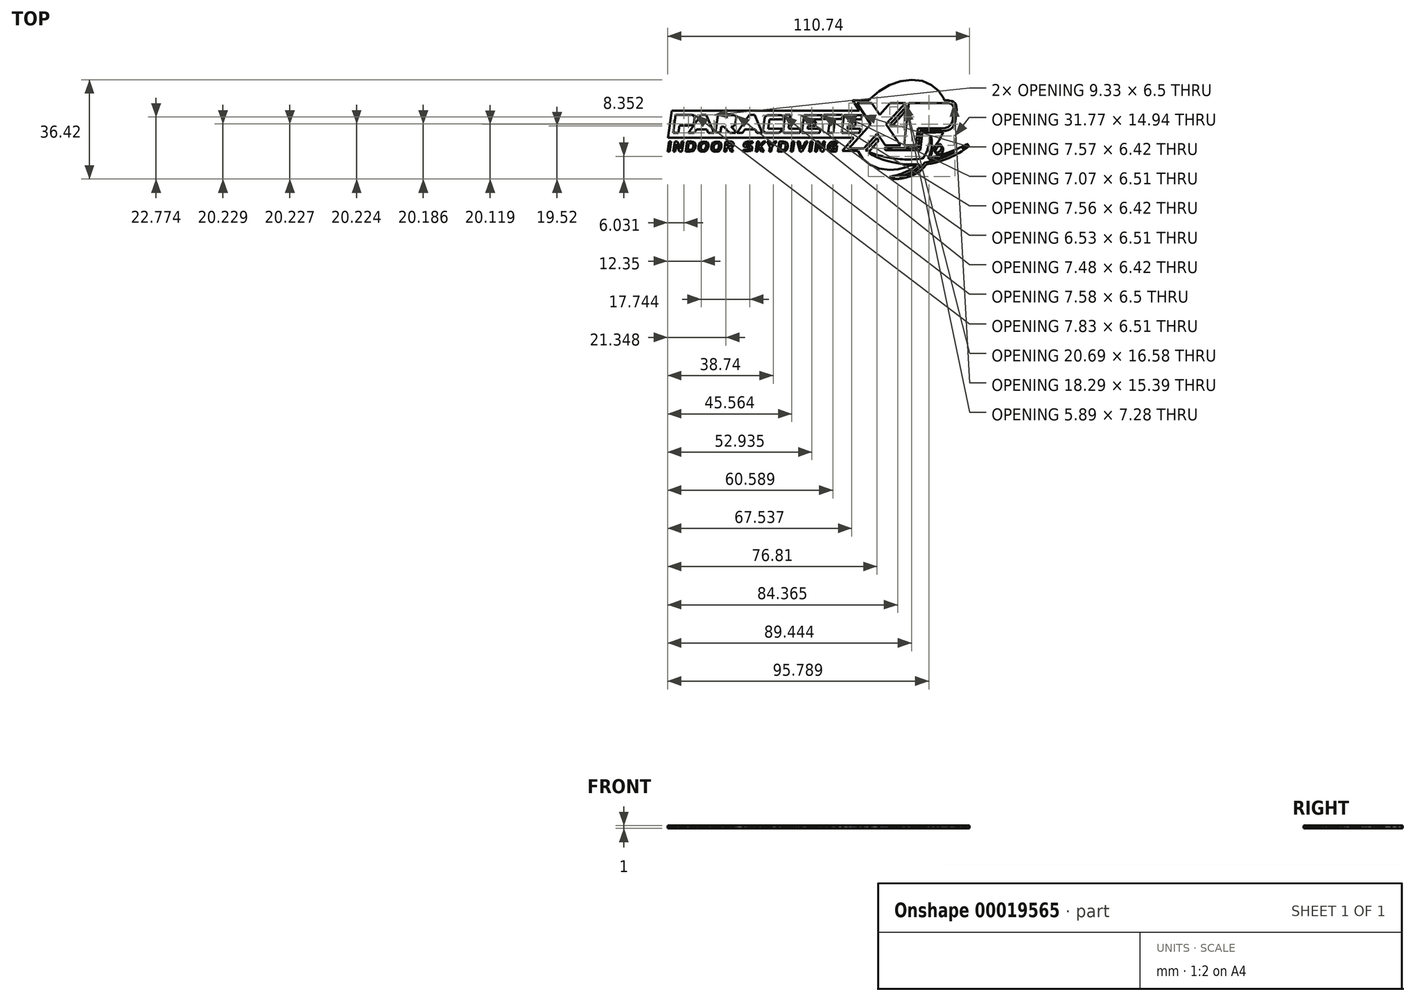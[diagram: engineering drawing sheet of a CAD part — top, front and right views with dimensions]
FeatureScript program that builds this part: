
annotation { "Feature Type Name" : "Feature", "Feature Type Description" : "" }
export const myFeature = defineFeature(function(context is Context, id is Id, definition is map)
    precondition{}
    {
        {
            var Q0;
            Q0=qCreatedBy(makeId("Top.planeOp"),FACE);
            var sketch = newSketch(context, id + "F0", { "sketchPlane" : qUnion([Q0])});
            skLineSegment(sketch, "E0", {"start": v(44.07, 4.06) * mm, "end": v(37.84, 4.06) * mm});
            skLineSegment(sketch, "E1", {"start": v(37.84, 4.06) * mm, "end": v(37.92, 4.76) * mm});
            skLineSegment(sketch, "E2", {"start": v(37.92, 4.76) * mm, "end": v(44.15, 4.76) * mm});
            skLineSegment(sketch, "E3", {"start": v(44.15, 4.76) * mm, "end": v(44.07, 4.06) * mm});
            skLineSegment(sketch, "E4", {"start": v(31.73, 6.48) * mm, "end": v(26.66, 0.92) * mm});
            skLineSegment(sketch, "E5", {"start": v(26.66, 0.92) * mm, "end": v(26.05, 1.81) * mm});
            skLineSegment(sketch, "E6", {"start": v(26.05, 1.81) * mm, "end": v(31.43, 7.64) * mm});
            skLineSegment(sketch, "E7", {"start": v(31.43, 7.64) * mm, "end": v(31.94, 8.2) * mm});
            skLineSegment(sketch, "E8", {"start": v(31.94, 8.2) * mm, "end": v(31.73, 6.48) * mm});
            skLineSegment(sketch, "E9", {"start": v(18.73, -7.82) * mm, "end": v(17.16, -7.8) * mm});
            skLineSegment(sketch, "E10", {"start": v(17.16, -7.8) * mm, "end": v(21.42, -3.2) * mm});
            skLineSegment(sketch, "E11", {"start": v(21.42, -3.2) * mm, "end": v(21.98, -4.02) * mm});
            skLineSegment(sketch, "E12", {"start": v(21.98, -4.02) * mm, "end": v(18.73, -7.82) * mm});
            skLineSegment(sketch, "E13", {"start": v(50.18, 9.35) * mm, "end": v(49.97, 9.6) * mm});
            skLineSegment(sketch, "E14", {"start": v(49.97, 9.6) * mm, "end": v(49.52, 9.98) * mm});
            skLineSegment(sketch, "E15", {"start": v(49.52, 9.98) * mm, "end": v(48.81, 10.37) * mm});
            skLineSegment(sketch, "E16", {"start": v(48.81, 10.37) * mm, "end": v(47.85, 10.6) * mm});
            skLineSegment(sketch, "E17", {"start": v(47.85, 10.6) * mm, "end": v(47.79, 10.6) * mm});
            skLineSegment(sketch, "E18", {"start": v(47.79, 10.6) * mm, "end": v(47.5, 10.6) * mm});
            skLineSegment(sketch, "E19", {"start": v(47.5, 10.6) * mm, "end": v(46.1, 10.64) * mm});
            skLineSegment(sketch, "E20", {"start": v(46.1, 10.64) * mm, "end": v(45.86, 11.32) * mm});
            skLineSegment(sketch, "E21", {"start": v(45.86, 11.32) * mm, "end": v(43.99, 14.14) * mm});
            skLineSegment(sketch, "E22", {"start": v(43.99, 14.14) * mm, "end": v(41.35, 16.31) * mm});
            skLineSegment(sketch, "E23", {"start": v(41.35, 16.31) * mm, "end": v(38.05, 17.72) * mm});
            skLineSegment(sketch, "E24", {"start": v(38.05, 17.72) * mm, "end": v(34.16, 18.21) * mm});
            skLineSegment(sketch, "E25", {"start": v(34.16, 18.21) * mm, "end": v(29.98, 17.7) * mm});
            skLineSegment(sketch, "E26", {"start": v(29.98, 17.7) * mm, "end": v(25.94, 16.25) * mm});
            skLineSegment(sketch, "E27", {"start": v(25.94, 16.25) * mm, "end": v(22.2, 14) * mm});
            skLineSegment(sketch, "E28", {"start": v(22.2, 14) * mm, "end": v(18.9, 11.11) * mm});
            skLineSegment(sketch, "E29", {"start": v(18.9, 11.11) * mm, "end": v(18.9, 11.11) * mm});
            skLineSegment(sketch, "E30", {"start": v(18.9, 11.11) * mm, "end": v(18.6, 10.65) * mm});
            skLineSegment(sketch, "E31", {"start": v(18.6, 10.65) * mm, "end": v(12.46, 10.63) * mm});
            skLineSegment(sketch, "E32", {"start": v(12.46, 10.63) * mm, "end": v(14.94, 6.88) * mm});
            skLineSegment(sketch, "E33", {"start": v(14.94, 6.88) * mm, "end": v(-53.8, 6.88) * mm});
            skLineSegment(sketch, "E34", {"start": v(-53.8, 6.88) * mm, "end": v(-55.18, -3) * mm});
            skLineSegment(sketch, "E35", {"start": v(-55.18, -3) * mm, "end": v(12.92, -3) * mm});
            skLineSegment(sketch, "E36", {"start": v(12.92, -3) * mm, "end": v(8.72, -7.94) * mm});
            skLineSegment(sketch, "E37", {"start": v(8.72, -7.94) * mm, "end": v(14.43, -7.94) * mm});
            skLineSegment(sketch, "E38", {"start": v(14.43, -7.94) * mm, "end": v(16.25, -10.8) * mm});
            skLineSegment(sketch, "E39", {"start": v(16.25, -10.8) * mm, "end": v(18.84, -12.99) * mm});
            skLineSegment(sketch, "E40", {"start": v(18.84, -12.99) * mm, "end": v(22.15, -14.38) * mm});
            skLineSegment(sketch, "E41", {"start": v(22.15, -14.38) * mm, "end": v(26.1, -14.87) * mm});
            skLineSegment(sketch, "E42", {"start": v(26.1, -14.87) * mm, "end": v(29.14, -14.6) * mm});
            skLineSegment(sketch, "E43", {"start": v(29.14, -14.6) * mm, "end": v(32.13, -13.8) * mm});
            skLineSegment(sketch, "E44", {"start": v(32.13, -13.8) * mm, "end": v(35.01, -12.55) * mm});
            skLineSegment(sketch, "E45", {"start": v(35.01, -12.55) * mm, "end": v(37.72, -10.88) * mm});
            skLineSegment(sketch, "E46", {"start": v(37.72, -10.88) * mm, "end": v(40.2, -8.85) * mm});
            skLineSegment(sketch, "E47", {"start": v(40.2, -8.85) * mm, "end": v(42.4, -6.5) * mm});
            skLineSegment(sketch, "E48", {"start": v(42.4, -6.5) * mm, "end": v(44.24, -3.9) * mm});
            skLineSegment(sketch, "E49", {"start": v(44.24, -3.9) * mm, "end": v(45.67, -1.08) * mm});
            skLineSegment(sketch, "E50", {"start": v(45.67, -1.08) * mm, "end": v(42.9, -1.08) * mm});
            skLineSegment(sketch, "E51", {"start": v(42.9, -1.08) * mm, "end": v(38, -1.1) * mm});
            skLineSegment(sketch, "E52", {"start": v(38, -1.1) * mm, "end": v(37.24, -7.58) * mm});
            skLineSegment(sketch, "E53", {"start": v(37.24, -7.58) * mm, "end": v(24.6, -7.58) * mm});
            skLineSegment(sketch, "E54", {"start": v(24.6, -7.58) * mm, "end": v(24.04, -6.88) * mm});
            skLineSegment(sketch, "E55", {"start": v(24.04, -6.88) * mm, "end": v(36.5, -6.88) * mm});
            skLineSegment(sketch, "E56", {"start": v(36.5, -6.88) * mm, "end": v(37.17, -0.53) * mm});
            skLineSegment(sketch, "E57", {"start": v(37.17, -0.53) * mm, "end": v(46.28, -0.53) * mm});
            skLineSegment(sketch, "E58", {"start": v(46.28, -0.53) * mm, "end": v(46.39, -0.53) * mm});
            skLineSegment(sketch, "E59", {"start": v(46.39, -0.53) * mm, "end": v(46.67, -0.51) * mm});
            skLineSegment(sketch, "E60", {"start": v(46.67, -0.51) * mm, "end": v(47.1, -0.44) * mm});
            skLineSegment(sketch, "E61", {"start": v(47.1, -0.44) * mm, "end": v(47.61, -0.28) * mm});
            skLineSegment(sketch, "E62", {"start": v(47.61, -0.28) * mm, "end": v(48.18, 0) * mm});
            skLineSegment(sketch, "E63", {"start": v(48.18, 0) * mm, "end": v(48.76, 0.43) * mm});
            skLineSegment(sketch, "E64", {"start": v(48.76, 0.43) * mm, "end": v(49.3, 1.05) * mm});
            skLineSegment(sketch, "E65", {"start": v(49.3, 1.05) * mm, "end": v(49.78, 1.89) * mm});
            skLineSegment(sketch, "E66", {"start": v(49.78, 1.89) * mm, "end": v(49.85, 2.07) * mm});
            skLineSegment(sketch, "E67", {"start": v(49.85, 2.07) * mm, "end": v(49.92, 2.23) * mm});
            skLineSegment(sketch, "E68", {"start": v(49.92, 2.23) * mm, "end": v(49.91, 2.22) * mm});
            skLineSegment(sketch, "E69", {"start": v(49.91, 2.22) * mm, "end": v(50.05, 2.78) * mm});
            skLineSegment(sketch, "E70", {"start": v(50.05, 2.78) * mm, "end": v(50.57, 7.29) * mm});
            skLineSegment(sketch, "E71", {"start": v(50.57, 7.29) * mm, "end": v(50.54, 8.36) * mm});
            skLineSegment(sketch, "E72", {"start": v(50.54, 8.36) * mm, "end": v(50.18, 9.35) * mm});
            skLineSegment(sketch, "E73", {"start": v(22.13, -1.6) * mm, "end": v(24.62, -5.2) * mm});
            skLineSegment(sketch, "E74", {"start": v(24.62, -5.2) * mm, "end": v(24.85, -5.3) * mm});
            skLineSegment(sketch, "E75", {"start": v(24.85, -5.3) * mm, "end": v(25.32, -5.3) * mm});
            skLineSegment(sketch, "E76", {"start": v(25.32, -5.3) * mm, "end": v(25, -4.84) * mm});
            skLineSegment(sketch, "E77", {"start": v(25, -4.84) * mm, "end": v(24.98, -4.84) * mm});
            skLineSegment(sketch, "E78", {"start": v(24.98, -4.84) * mm, "end": v(22.48, -1.22) * mm});
            skLineSegment(sketch, "E79", {"start": v(22.48, -1.22) * mm, "end": v(22.13, -1.6) * mm});
            skLineSegment(sketch, "E80", {"start": v(19.54, 8.64) * mm, "end": v(19.3, 9) * mm});
            skLineSegment(sketch, "E81", {"start": v(19.3, 9) * mm, "end": v(19.08, 9.12) * mm});
            skLineSegment(sketch, "E82", {"start": v(19.08, 9.12) * mm, "end": v(15.47, 9.12) * mm});
            skLineSegment(sketch, "E83", {"start": v(15.47, 9.12) * mm, "end": v(15.19, 8.96) * mm});
            skLineSegment(sketch, "E84", {"start": v(15.19, 8.96) * mm, "end": v(15.19, 8.64) * mm});
            skLineSegment(sketch, "E85", {"start": v(15.19, 8.64) * mm, "end": v(16.41, 6.85) * mm});
            skLineSegment(sketch, "E86", {"start": v(16.41, 6.85) * mm, "end": v(17.03, 6.85) * mm});
            skLineSegment(sketch, "E87", {"start": v(17.03, 6.85) * mm, "end": v(15.8, 8.64) * mm});
            skLineSegment(sketch, "E88", {"start": v(15.8, 8.64) * mm, "end": v(19.54, 8.64) * mm});
            skLineSegment(sketch, "E89", {"start": v(30.36, 8.64) * mm, "end": v(30.43, 8.96) * mm});
            skLineSegment(sketch, "E90", {"start": v(30.43, 8.96) * mm, "end": v(30.19, 9.12) * mm});
            skLineSegment(sketch, "E91", {"start": v(30.19, 9.12) * mm, "end": v(26.6, 9.12) * mm});
            skLineSegment(sketch, "E92", {"start": v(26.6, 9.12) * mm, "end": v(26.34, 9) * mm});
            skLineSegment(sketch, "E93", {"start": v(26.34, 9) * mm, "end": v(14.22, -4.18) * mm});
            skLineSegment(sketch, "E94", {"start": v(14.22, -4.18) * mm, "end": v(14.19, -4.45) * mm});
            skLineSegment(sketch, "E95", {"start": v(14.19, -4.45) * mm, "end": v(14.2, -4.48) * mm});
            skLineSegment(sketch, "E96", {"start": v(14.2, -4.48) * mm, "end": v(14.37, -4.56) * mm});
            skLineSegment(sketch, "E97", {"start": v(14.37, -4.56) * mm, "end": v(14.55, -4.48) * mm});
            skLineSegment(sketch, "E98", {"start": v(14.55, -4.48) * mm, "end": v(26.61, 8.64) * mm});
            skLineSegment(sketch, "E99", {"start": v(26.61, 8.64) * mm, "end": v(30.36, 8.64) * mm});
            skLineSegment(sketch, "E100", {"start": v(12.17, -5.78) * mm, "end": v(19.17, 1.9) * mm});
            skLineSegment(sketch, "E101", {"start": v(19.17, 1.9) * mm, "end": v(14.04, 9.6) * mm});
            skLineSegment(sketch, "E102", {"start": v(14.04, 9.6) * mm, "end": v(19.5, 9.6) * mm});
            skLineSegment(sketch, "E103", {"start": v(19.5, 9.6) * mm, "end": v(22.39, 5.38) * mm});
            skLineSegment(sketch, "E104", {"start": v(22.39, 5.38) * mm, "end": v(26.27, 9.6) * mm});
            skLineSegment(sketch, "E105", {"start": v(26.27, 9.6) * mm, "end": v(31.79, 9.6) * mm});
            skLineSegment(sketch, "E106", {"start": v(31.79, 9.6) * mm, "end": v(31.13, 8.83) * mm});
            skLineSegment(sketch, "E107", {"start": v(31.13, 8.83) * mm, "end": v(30.69, 8.34) * mm});
            skLineSegment(sketch, "E108", {"start": v(30.69, 8.34) * mm, "end": v(24.75, 1.9) * mm});
            skLineSegment(sketch, "E109", {"start": v(24.75, 1.9) * mm, "end": v(30.01, -5.78) * mm});
            skLineSegment(sketch, "E110", {"start": v(30.01, -5.78) * mm, "end": v(24.42, -5.78) * mm});
            skLineSegment(sketch, "E111", {"start": v(24.42, -5.78) * mm, "end": v(21.55, -1.57) * mm});
            skLineSegment(sketch, "E112", {"start": v(21.55, -1.57) * mm, "end": v(17.65, -5.78) * mm});
            skLineSegment(sketch, "E113", {"start": v(17.65, -5.78) * mm, "end": v(12.17, -5.78) * mm});
            skLineSegment(sketch, "E114", {"start": v(37.01, 5.7) * mm, "end": v(36.69, 3.02) * mm});
            skLineSegment(sketch, "E115", {"start": v(36.69, 3.02) * mm, "end": v(44.2, 3.02) * mm});
            skLineSegment(sketch, "E116", {"start": v(44.2, 3.02) * mm, "end": v(44.8, 3.21) * mm});
            skLineSegment(sketch, "E117", {"start": v(44.8, 3.21) * mm, "end": v(45.07, 3.8) * mm});
            skLineSegment(sketch, "E118", {"start": v(45.07, 3.8) * mm, "end": v(45.2, 4.92) * mm});
            skLineSegment(sketch, "E119", {"start": v(45.2, 4.92) * mm, "end": v(45.08, 5.51) * mm});
            skLineSegment(sketch, "E120", {"start": v(45.08, 5.51) * mm, "end": v(44.53, 5.7) * mm});
            skLineSegment(sketch, "E121", {"start": v(44.53, 5.7) * mm, "end": v(37.01, 5.7) * mm});
            skLineSegment(sketch, "E122", {"start": v(44.95, 2.82) * mm, "end": v(44.15, 2.55) * mm});
            skLineSegment(sketch, "E123", {"start": v(44.15, 2.55) * mm, "end": v(36.85, 2.55) * mm});
            skLineSegment(sketch, "E124", {"start": v(36.85, 2.55) * mm, "end": v(36.6, 2.34) * mm});
            skLineSegment(sketch, "E125", {"start": v(36.6, 2.34) * mm, "end": v(36.6, 2.29) * mm});
            skLineSegment(sketch, "E126", {"start": v(36.6, 2.29) * mm, "end": v(36.79, 2.07) * mm});
            skLineSegment(sketch, "E127", {"start": v(36.79, 2.07) * mm, "end": v(44.1, 2.07) * mm});
            skLineSegment(sketch, "E128", {"start": v(44.1, 2.07) * mm, "end": v(44.68, 2.26) * mm});
            skLineSegment(sketch, "E129", {"start": v(44.68, 2.26) * mm, "end": v(44.95, 2.82) * mm});
            skLineSegment(sketch, "E130", {"start": v(49.06, 7.83) * mm, "end": v(48.53, 8.8) * mm});
            skLineSegment(sketch, "E131", {"start": v(48.53, 8.8) * mm, "end": v(47.46, 9.12) * mm});
            skLineSegment(sketch, "E132", {"start": v(47.46, 9.12) * mm, "end": v(33.77, 9.12) * mm});
            skLineSegment(sketch, "E133", {"start": v(33.77, 9.12) * mm, "end": v(33.53, 8.9) * mm});
            skLineSegment(sketch, "E134", {"start": v(33.53, 8.9) * mm, "end": v(33.52, 8.86) * mm});
            skLineSegment(sketch, "E135", {"start": v(33.52, 8.86) * mm, "end": v(33.52, 8.83) * mm});
            skLineSegment(sketch, "E136", {"start": v(33.52, 8.83) * mm, "end": v(33.35, 7.43) * mm});
            skLineSegment(sketch, "E137", {"start": v(33.35, 7.43) * mm, "end": v(33.54, 7.22) * mm});
            skLineSegment(sketch, "E138", {"start": v(33.54, 7.22) * mm, "end": v(33.6, 7.22) * mm});
            skLineSegment(sketch, "E139", {"start": v(33.6, 7.22) * mm, "end": v(33.83, 7.43) * mm});
            skLineSegment(sketch, "E140", {"start": v(33.83, 7.43) * mm, "end": v(33.98, 8.64) * mm});
            skLineSegment(sketch, "E141", {"start": v(33.98, 8.64) * mm, "end": v(47.43, 8.64) * mm});
            skLineSegment(sketch, "E142", {"start": v(47.43, 8.64) * mm, "end": v(48.37, 8.43) * mm});
            skLineSegment(sketch, "E143", {"start": v(48.37, 8.43) * mm, "end": v(49.06, 7.83) * mm});
            skLineSegment(sketch, "E144", {"start": v(45.06, 0.41) * mm, "end": v(42.1, 0.43) * mm});
            skLineSegment(sketch, "E145", {"start": v(42.1, 0.43) * mm, "end": v(36.38, 0.43) * mm});
            skLineSegment(sketch, "E146", {"start": v(36.38, 0.43) * mm, "end": v(35.63, -5.78) * mm});
            skLineSegment(sketch, "E147", {"start": v(35.63, -5.78) * mm, "end": v(31.28, -5.78) * mm});
            skLineSegment(sketch, "E148", {"start": v(31.28, -5.78) * mm, "end": v(33.13, 9.6) * mm});
            skLineSegment(sketch, "E149", {"start": v(33.13, 9.6) * mm, "end": v(47.52, 9.6) * mm});
            skLineSegment(sketch, "E150", {"start": v(47.52, 9.6) * mm, "end": v(48.38, 9.43) * mm});
            skLineSegment(sketch, "E151", {"start": v(48.38, 9.43) * mm, "end": v(49.07, 8.91) * mm});
            skLineSegment(sketch, "E152", {"start": v(49.07, 8.91) * mm, "end": v(49.5, 8.16) * mm});
            skLineSegment(sketch, "E153", {"start": v(49.5, 8.16) * mm, "end": v(49.56, 7.28) * mm});
            skLineSegment(sketch, "E154", {"start": v(49.56, 7.28) * mm, "end": v(49.03, 2.9) * mm});
            skLineSegment(sketch, "E155", {"start": v(49.03, 2.9) * mm, "end": v(48.5, 1.75) * mm});
            skLineSegment(sketch, "E156", {"start": v(48.5, 1.75) * mm, "end": v(47.54, 0.89) * mm});
            skLineSegment(sketch, "E157", {"start": v(47.54, 0.89) * mm, "end": v(47.5, 0.86) * mm});
            skLineSegment(sketch, "E158", {"start": v(47.5, 0.86) * mm, "end": v(46.46, 0.52) * mm});
            skLineSegment(sketch, "E159", {"start": v(46.46, 0.52) * mm, "end": v(45.06, 0.41) * mm});
            skLineSegment(sketch, "E160", {"start": v(11.1, -6.98) * mm, "end": v(19.17, 1.9) * mm});
            skLineSegment(sketch, "E161", {"start": v(21.55, -1.57) * mm, "end": v(16.57, -6.98) * mm});
            skLineSegment(sketch, "E162", {"start": v(16.57, -6.98) * mm, "end": v(11.1, -6.98) * mm});
            skLineSegment(sketch, "E163", {"start": v(-47.4, 2.4) * mm, "end": v(-47.75, 2.3) * mm});
            skLineSegment(sketch, "E164", {"start": v(-47.75, 2.3) * mm, "end": v(-50.84, 2.3) * mm});
            skLineSegment(sketch, "E165", {"start": v(-50.84, 2.3) * mm, "end": v(-50.94, 2.2) * mm});
            skLineSegment(sketch, "E166", {"start": v(-50.94, 2.2) * mm, "end": v(-50.94, 2.18) * mm});
            skLineSegment(sketch, "E167", {"start": v(-50.94, 2.18) * mm, "end": v(-50.86, 2.09) * mm});
            skLineSegment(sketch, "E168", {"start": v(-50.86, 2.09) * mm, "end": v(-47.77, 2.09) * mm});
            skLineSegment(sketch, "E169", {"start": v(-47.77, 2.09) * mm, "end": v(-47.4, 2.4) * mm});
            skLineSegment(sketch, "E170", {"start": v(-50.74, 3.62) * mm, "end": v(-50.9, 2.49) * mm});
            skLineSegment(sketch, "E171", {"start": v(-50.9, 2.49) * mm, "end": v(-47.72, 2.49) * mm});
            skLineSegment(sketch, "E172", {"start": v(-47.72, 2.49) * mm, "end": v(-47.35, 2.82) * mm});
            skLineSegment(sketch, "E173", {"start": v(-47.35, 2.82) * mm, "end": v(-47.28, 3.3) * mm});
            skLineSegment(sketch, "E174", {"start": v(-47.28, 3.3) * mm, "end": v(-47.56, 3.62) * mm});
            skLineSegment(sketch, "E175", {"start": v(-47.56, 3.62) * mm, "end": v(-50.74, 3.62) * mm});
            skLineSegment(sketch, "E176", {"start": v(-45.63, 4.53) * mm, "end": v(-45.85, 4.94) * mm});
            skLineSegment(sketch, "E177", {"start": v(-45.85, 4.94) * mm, "end": v(-46.3, 5.07) * mm});
            skLineSegment(sketch, "E178", {"start": v(-46.3, 5.07) * mm, "end": v(-52.09, 5.07) * mm});
            skLineSegment(sketch, "E179", {"start": v(-52.09, 5.07) * mm, "end": v(-52.19, 4.98) * mm});
            skLineSegment(sketch, "E180", {"start": v(-52.19, 4.98) * mm, "end": v(-52.2, 4.96) * mm});
            skLineSegment(sketch, "E181", {"start": v(-52.2, 4.96) * mm, "end": v(-52.2, 4.95) * mm});
            skLineSegment(sketch, "E182", {"start": v(-52.2, 4.95) * mm, "end": v(-52.28, 4.36) * mm});
            skLineSegment(sketch, "E183", {"start": v(-52.28, 4.36) * mm, "end": v(-52.2, 4.26) * mm});
            skLineSegment(sketch, "E184", {"start": v(-52.2, 4.26) * mm, "end": v(-52.18, 4.26) * mm});
            skLineSegment(sketch, "E185", {"start": v(-52.18, 4.26) * mm, "end": v(-52.08, 4.36) * mm});
            skLineSegment(sketch, "E186", {"start": v(-52.08, 4.36) * mm, "end": v(-52, 4.87) * mm});
            skLineSegment(sketch, "E187", {"start": v(-52, 4.87) * mm, "end": v(-46.31, 4.87) * mm});
            skLineSegment(sketch, "E188", {"start": v(-46.31, 4.87) * mm, "end": v(-45.63, 4.53) * mm});
            skLineSegment(sketch, "E189", {"start": v(-47.38, 1.39) * mm, "end": v(-48.63, 1.4) * mm});
            skLineSegment(sketch, "E190", {"start": v(-48.63, 1.4) * mm, "end": v(-51.05, 1.4) * mm});
            skLineSegment(sketch, "E191", {"start": v(-51.05, 1.4) * mm, "end": v(-51.42, -1.23) * mm});
            skLineSegment(sketch, "E192", {"start": v(-51.42, -1.23) * mm, "end": v(-53.26, -1.23) * mm});
            skLineSegment(sketch, "E193", {"start": v(-53.26, -1.23) * mm, "end": v(-52.35, 5.27) * mm});
            skLineSegment(sketch, "E194", {"start": v(-52.35, 5.27) * mm, "end": v(-46.27, 5.27) * mm});
            skLineSegment(sketch, "E195", {"start": v(-46.27, 5.27) * mm, "end": v(-45.62, 4.98) * mm});
            skLineSegment(sketch, "E196", {"start": v(-45.62, 4.98) * mm, "end": v(-45.42, 4.3) * mm});
            skLineSegment(sketch, "E197", {"start": v(-45.42, 4.3) * mm, "end": v(-45.68, 2.44) * mm});
            skLineSegment(sketch, "E198", {"start": v(-45.68, 2.44) * mm, "end": v(-45.92, 1.95) * mm});
            skLineSegment(sketch, "E199", {"start": v(-45.92, 1.95) * mm, "end": v(-46.33, 1.59) * mm});
            skLineSegment(sketch, "E200", {"start": v(-46.33, 1.59) * mm, "end": v(-46.34, 1.58) * mm});
            skLineSegment(sketch, "E201", {"start": v(-46.34, 1.58) * mm, "end": v(-47.38, 1.39) * mm});
            skLineSegment(sketch, "E202", {"start": v(-42.4, 3.25) * mm, "end": v(-43.63, 1.53) * mm});
            skLineSegment(sketch, "E203", {"start": v(-43.63, 1.53) * mm, "end": v(-41.64, 1.53) * mm});
            skLineSegment(sketch, "E204", {"start": v(-41.64, 1.53) * mm, "end": v(-42.4, 3.25) * mm});
            skLineSegment(sketch, "E205", {"start": v(-41.6, 1.33) * mm, "end": v(-43.7, 1.33) * mm});
            skLineSegment(sketch, "E206", {"start": v(-43.7, 1.33) * mm, "end": v(-43.79, 1.29) * mm});
            skLineSegment(sketch, "E207", {"start": v(-43.79, 1.29) * mm, "end": v(-43.8, 1.27) * mm});
            skLineSegment(sketch, "E208", {"start": v(-43.8, 1.27) * mm, "end": v(-43.81, 1.18) * mm});
            skLineSegment(sketch, "E209", {"start": v(-43.81, 1.18) * mm, "end": v(-43.74, 1.13) * mm});
            skLineSegment(sketch, "E210", {"start": v(-43.74, 1.13) * mm, "end": v(-41.62, 1.13) * mm});
            skLineSegment(sketch, "E211", {"start": v(-41.62, 1.13) * mm, "end": v(-41.54, 1.18) * mm});
            skLineSegment(sketch, "E212", {"start": v(-41.54, 1.18) * mm, "end": v(-41.53, 1.27) * mm});
            skLineSegment(sketch, "E213", {"start": v(-41.53, 1.27) * mm, "end": v(-41.54, 1.29) * mm});
            skLineSegment(sketch, "E214", {"start": v(-41.54, 1.29) * mm, "end": v(-41.6, 1.33) * mm});
            skLineSegment(sketch, "E215", {"start": v(-47.07, -0.7) * mm, "end": v(-47.08, -0.79) * mm});
            skLineSegment(sketch, "E216", {"start": v(-47.08, -0.79) * mm, "end": v(-47, -0.83) * mm});
            skLineSegment(sketch, "E217", {"start": v(-47, -0.83) * mm, "end": v(-46.99, -0.83) * mm});
            skLineSegment(sketch, "E218", {"start": v(-46.99, -0.83) * mm, "end": v(-46.9, -0.79) * mm});
            skLineSegment(sketch, "E219", {"start": v(-46.9, -0.79) * mm, "end": v(-42.85, 4.86) * mm});
            skLineSegment(sketch, "E220", {"start": v(-42.85, 4.86) * mm, "end": v(-41.55, 4.86) * mm});
            skLineSegment(sketch, "E221", {"start": v(-41.55, 4.86) * mm, "end": v(-41.46, 4.9) * mm});
            skLineSegment(sketch, "E222", {"start": v(-41.46, 4.9) * mm, "end": v(-41.45, 4.93) * mm});
            skLineSegment(sketch, "E223", {"start": v(-41.45, 4.93) * mm, "end": v(-41.43, 5.02) * mm});
            skLineSegment(sketch, "E224", {"start": v(-41.43, 5.02) * mm, "end": v(-41.5, 5.06) * mm});
            skLineSegment(sketch, "E225", {"start": v(-41.5, 5.06) * mm, "end": v(-42.94, 5.06) * mm});
            skLineSegment(sketch, "E226", {"start": v(-42.94, 5.06) * mm, "end": v(-47.07, -0.7) * mm});
            skLineSegment(sketch, "E227", {"start": v(-40.99, 0.03) * mm, "end": v(-44.7, 0.03) * mm});
            skLineSegment(sketch, "E228", {"start": v(-44.7, 0.03) * mm, "end": v(-45.61, -1.23) * mm});
            skLineSegment(sketch, "E229", {"start": v(-45.61, -1.23) * mm, "end": v(-47.68, -1.23) * mm});
            skLineSegment(sketch, "E230", {"start": v(-47.68, -1.23) * mm, "end": v(-43.03, 5.27) * mm});
            skLineSegment(sketch, "E231", {"start": v(-43.03, 5.27) * mm, "end": v(-41.2, 5.27) * mm});
            skLineSegment(sketch, "E232", {"start": v(-41.2, 5.27) * mm, "end": v(-38.36, -1.23) * mm});
            skLineSegment(sketch, "E233", {"start": v(-38.36, -1.23) * mm, "end": v(-40.44, -1.23) * mm});
            skLineSegment(sketch, "E234", {"start": v(-40.44, -1.23) * mm, "end": v(-40.99, 0.03) * mm});
            skLineSegment(sketch, "E235", {"start": v(-30.67, -1.03) * mm, "end": v(-30.57, -0.95) * mm});
            skLineSegment(sketch, "E236", {"start": v(-30.57, -0.95) * mm, "end": v(-30.59, -0.81) * mm});
            skLineSegment(sketch, "E237", {"start": v(-30.59, -0.81) * mm, "end": v(-31.33, -0.04) * mm});
            skLineSegment(sketch, "E238", {"start": v(-31.33, -0.04) * mm, "end": v(-32.13, 0.8) * mm});
            skLineSegment(sketch, "E239", {"start": v(-32.13, 0.8) * mm, "end": v(-32.44, 0.8) * mm});
            skLineSegment(sketch, "E240", {"start": v(-32.44, 0.8) * mm, "end": v(-31.87, 0.2) * mm});
            skLineSegment(sketch, "E241", {"start": v(-31.87, 0.2) * mm, "end": v(-30.87, -0.83) * mm});
            skLineSegment(sketch, "E242", {"start": v(-30.87, -0.83) * mm, "end": v(-30.67, -1.03) * mm});
            skLineSegment(sketch, "E243", {"start": v(-32.22, 2.15) * mm, "end": v(-32.39, 2.12) * mm});
            skLineSegment(sketch, "E244", {"start": v(-32.39, 2.12) * mm, "end": v(-35.43, 2.12) * mm});
            skLineSegment(sketch, "E245", {"start": v(-35.43, 2.12) * mm, "end": v(-35.53, 2.02) * mm});
            skLineSegment(sketch, "E246", {"start": v(-35.53, 2.02) * mm, "end": v(-35.53, 2) * mm});
            skLineSegment(sketch, "E247", {"start": v(-35.53, 2) * mm, "end": v(-35.45, 1.91) * mm});
            skLineSegment(sketch, "E248", {"start": v(-35.45, 1.91) * mm, "end": v(-32.41, 1.91) * mm});
            skLineSegment(sketch, "E249", {"start": v(-32.41, 1.91) * mm, "end": v(-32.23, 2.08) * mm});
            skLineSegment(sketch, "E250", {"start": v(-32.23, 2.08) * mm, "end": v(-32.22, 2.15) * mm});
            skLineSegment(sketch, "E251", {"start": v(-35.29, 3.75) * mm, "end": v(-35.49, 2.32) * mm});
            skLineSegment(sketch, "E252", {"start": v(-35.49, 2.32) * mm, "end": v(-32.36, 2.32) * mm});
            skLineSegment(sketch, "E253", {"start": v(-32.36, 2.32) * mm, "end": v(-32.18, 2.48) * mm});
            skLineSegment(sketch, "E254", {"start": v(-32.18, 2.48) * mm, "end": v(-32.02, 3.58) * mm});
            skLineSegment(sketch, "E255", {"start": v(-32.02, 3.58) * mm, "end": v(-32.16, 3.75) * mm});
            skLineSegment(sketch, "E256", {"start": v(-32.16, 3.75) * mm, "end": v(-35.29, 3.75) * mm});
            skLineSegment(sketch, "E257", {"start": v(-30.44, 4.52) * mm, "end": v(-30.65, 4.92) * mm});
            skLineSegment(sketch, "E258", {"start": v(-30.65, 4.92) * mm, "end": v(-31.1, 5.06) * mm});
            skLineSegment(sketch, "E259", {"start": v(-31.1, 5.06) * mm, "end": v(-36.65, 5.06) * mm});
            skLineSegment(sketch, "E260", {"start": v(-36.65, 5.06) * mm, "end": v(-36.76, 4.97) * mm});
            skLineSegment(sketch, "E261", {"start": v(-36.76, 4.97) * mm, "end": v(-36.76, 4.95) * mm});
            skLineSegment(sketch, "E262", {"start": v(-36.76, 4.95) * mm, "end": v(-36.68, 4.86) * mm});
            skLineSegment(sketch, "E263", {"start": v(-36.68, 4.86) * mm, "end": v(-31.11, 4.86) * mm});
            skLineSegment(sketch, "E264", {"start": v(-31.11, 4.86) * mm, "end": v(-30.44, 4.52) * mm});
            skLineSegment(sketch, "E265", {"start": v(-37.81, -1.17) * mm, "end": v(-36.92, 5.26) * mm});
            skLineSegment(sketch, "E266", {"start": v(-36.92, 5.26) * mm, "end": v(-31.07, 5.26) * mm});
            skLineSegment(sketch, "E267", {"start": v(-31.07, 5.26) * mm, "end": v(-30.42, 4.97) * mm});
            skLineSegment(sketch, "E268", {"start": v(-30.42, 4.97) * mm, "end": v(-30.23, 4.28) * mm});
            skLineSegment(sketch, "E269", {"start": v(-30.23, 4.28) * mm, "end": v(-30.55, 1.98) * mm});
            skLineSegment(sketch, "E270", {"start": v(-30.55, 1.98) * mm, "end": v(-30.94, 1.28) * mm});
            skLineSegment(sketch, "E271", {"start": v(-30.94, 1.28) * mm, "end": v(-31.67, 1) * mm});
            skLineSegment(sketch, "E272", {"start": v(-31.67, 1) * mm, "end": v(-32.04, 1) * mm});
            skLineSegment(sketch, "E273", {"start": v(-32.04, 1) * mm, "end": v(-31.52, 0.46) * mm});
            skLineSegment(sketch, "E274", {"start": v(-31.52, 0.46) * mm, "end": v(-30.4, -0.7) * mm});
            skLineSegment(sketch, "E275", {"start": v(-30.4, -0.7) * mm, "end": v(-30.47, -1.23) * mm});
            skLineSegment(sketch, "E276", {"start": v(-30.47, -1.23) * mm, "end": v(-32.58, -1.23) * mm});
            skLineSegment(sketch, "E277", {"start": v(-32.58, -1.23) * mm, "end": v(-34.74, 1) * mm});
            skLineSegment(sketch, "E278", {"start": v(-34.74, 1) * mm, "end": v(-35.67, 1) * mm});
            skLineSegment(sketch, "E279", {"start": v(-35.67, 1) * mm, "end": v(-35.97, -1.17) * mm});
            skLineSegment(sketch, "E280", {"start": v(-35.97, -1.17) * mm, "end": v(-37.81, -1.17) * mm});
            skLineSegment(sketch, "E281", {"start": v(-24.65, 3.25) * mm, "end": v(-25.89, 1.53) * mm});
            skLineSegment(sketch, "E282", {"start": v(-25.89, 1.53) * mm, "end": v(-23.9, 1.53) * mm});
            skLineSegment(sketch, "E283", {"start": v(-23.9, 1.53) * mm, "end": v(-24.65, 3.25) * mm});
            skLineSegment(sketch, "E284", {"start": v(-23.87, 1.33) * mm, "end": v(-25.96, 1.33) * mm});
            skLineSegment(sketch, "E285", {"start": v(-25.96, 1.33) * mm, "end": v(-26.04, 1.29) * mm});
            skLineSegment(sketch, "E286", {"start": v(-26.04, 1.29) * mm, "end": v(-26.06, 1.27) * mm});
            skLineSegment(sketch, "E287", {"start": v(-26.06, 1.27) * mm, "end": v(-26.07, 1.18) * mm});
            skLineSegment(sketch, "E288", {"start": v(-26.07, 1.18) * mm, "end": v(-26, 1.13) * mm});
            skLineSegment(sketch, "E289", {"start": v(-26, 1.13) * mm, "end": v(-23.88, 1.13) * mm});
            skLineSegment(sketch, "E290", {"start": v(-23.88, 1.13) * mm, "end": v(-23.8, 1.18) * mm});
            skLineSegment(sketch, "E291", {"start": v(-23.8, 1.18) * mm, "end": v(-23.78, 1.27) * mm});
            skLineSegment(sketch, "E292", {"start": v(-23.78, 1.27) * mm, "end": v(-23.8, 1.29) * mm});
            skLineSegment(sketch, "E293", {"start": v(-23.8, 1.29) * mm, "end": v(-23.87, 1.33) * mm});
            skLineSegment(sketch, "E294", {"start": v(-29.33, -0.7) * mm, "end": v(-29.34, -0.79) * mm});
            skLineSegment(sketch, "E295", {"start": v(-29.34, -0.79) * mm, "end": v(-29.27, -0.83) * mm});
            skLineSegment(sketch, "E296", {"start": v(-29.27, -0.83) * mm, "end": v(-29.24, -0.83) * mm});
            skLineSegment(sketch, "E297", {"start": v(-29.24, -0.83) * mm, "end": v(-29.16, -0.79) * mm});
            skLineSegment(sketch, "E298", {"start": v(-29.16, -0.79) * mm, "end": v(-25.1, 4.86) * mm});
            skLineSegment(sketch, "E299", {"start": v(-25.1, 4.86) * mm, "end": v(-23.8, 4.86) * mm});
            skLineSegment(sketch, "E300", {"start": v(-23.8, 4.86) * mm, "end": v(-23.72, 4.9) * mm});
            skLineSegment(sketch, "E301", {"start": v(-23.72, 4.9) * mm, "end": v(-23.7, 4.93) * mm});
            skLineSegment(sketch, "E302", {"start": v(-23.7, 4.93) * mm, "end": v(-23.69, 5.02) * mm});
            skLineSegment(sketch, "E303", {"start": v(-23.69, 5.02) * mm, "end": v(-23.76, 5.06) * mm});
            skLineSegment(sketch, "E304", {"start": v(-23.76, 5.06) * mm, "end": v(-25.2, 5.06) * mm});
            skLineSegment(sketch, "E305", {"start": v(-25.2, 5.06) * mm, "end": v(-29.33, -0.7) * mm});
            skLineSegment(sketch, "E306", {"start": v(-23.24, 0.03) * mm, "end": v(-26.96, 0.03) * mm});
            skLineSegment(sketch, "E307", {"start": v(-26.96, 0.03) * mm, "end": v(-27.87, -1.23) * mm});
            skLineSegment(sketch, "E308", {"start": v(-27.87, -1.23) * mm, "end": v(-29.94, -1.23) * mm});
            skLineSegment(sketch, "E309", {"start": v(-29.94, -1.23) * mm, "end": v(-25.29, 5.27) * mm});
            skLineSegment(sketch, "E310", {"start": v(-25.29, 5.27) * mm, "end": v(-23.46, 5.27) * mm});
            skLineSegment(sketch, "E311", {"start": v(-23.46, 5.27) * mm, "end": v(-20.61, -1.23) * mm});
            skLineSegment(sketch, "E312", {"start": v(-20.61, -1.23) * mm, "end": v(-22.7, -1.23) * mm});
            skLineSegment(sketch, "E313", {"start": v(-22.7, -1.23) * mm, "end": v(-23.24, 0.03) * mm});
            skLineSegment(sketch, "E314", {"start": v(-18.58, 0.09) * mm, "end": v(-18.7, -0.01) * mm});
            skLineSegment(sketch, "E315", {"start": v(-18.7, -0.01) * mm, "end": v(-18.61, -0.12) * mm});
            skLineSegment(sketch, "E316", {"start": v(-18.61, -0.12) * mm, "end": v(-13.71, -0.12) * mm});
            skLineSegment(sketch, "E317", {"start": v(-13.71, -0.12) * mm, "end": v(-13.6, -0.01) * mm});
            skLineSegment(sketch, "E318", {"start": v(-13.6, -0.01) * mm, "end": v(-13.69, 0.09) * mm});
            skLineSegment(sketch, "E319", {"start": v(-13.69, 0.09) * mm, "end": v(-18.58, 0.09) * mm});
            skLineSegment(sketch, "E320", {"start": v(-13.27, 4.8) * mm, "end": v(-13.76, 5) * mm});
            skLineSegment(sketch, "E321", {"start": v(-13.76, 5) * mm, "end": v(-18.58, 5) * mm});
            skLineSegment(sketch, "E322", {"start": v(-18.58, 5) * mm, "end": v(-18.7, 4.89) * mm});
            skLineSegment(sketch, "E323", {"start": v(-18.7, 4.89) * mm, "end": v(-18.61, 4.8) * mm});
            skLineSegment(sketch, "E324", {"start": v(-18.61, 4.8) * mm, "end": v(-13.27, 4.8) * mm});
            skLineSegment(sketch, "E325", {"start": v(-19.55, 4.2) * mm, "end": v(-19.46, 4.1) * mm});
            skLineSegment(sketch, "E326", {"start": v(-19.46, 4.1) * mm, "end": v(-19.35, 4.2) * mm});
            skLineSegment(sketch, "E327", {"start": v(-19.35, 4.2) * mm, "end": v(-18.89, 4.75) * mm});
            skLineSegment(sketch, "E328", {"start": v(-18.89, 4.75) * mm, "end": v(-18.8, 4.88) * mm});
            skLineSegment(sketch, "E329", {"start": v(-18.8, 4.88) * mm, "end": v(-18.92, 4.95) * mm});
            skLineSegment(sketch, "E330", {"start": v(-18.92, 4.95) * mm, "end": v(-18.93, 4.94) * mm});
            skLineSegment(sketch, "E331", {"start": v(-18.93, 4.94) * mm, "end": v(-19.36, 4.67) * mm});
            skLineSegment(sketch, "E332", {"start": v(-19.36, 4.67) * mm, "end": v(-19.55, 4.2) * mm});
            skLineSegment(sketch, "E333", {"start": v(-19.52, -1.23) * mm, "end": v(-20.18, -0.95) * mm});
            skLineSegment(sketch, "E334", {"start": v(-20.18, -0.95) * mm, "end": v(-20.37, -0.25) * mm});
            skLineSegment(sketch, "E335", {"start": v(-20.37, -0.25) * mm, "end": v(-19.75, 4.2) * mm});
            skLineSegment(sketch, "E336", {"start": v(-19.75, 4.2) * mm, "end": v(-19.36, 4.9) * mm});
            skLineSegment(sketch, "E337", {"start": v(-19.36, 4.9) * mm, "end": v(-18.63, 5.19) * mm});
            skLineSegment(sketch, "E338", {"start": v(-18.63, 5.19) * mm, "end": v(-13.74, 5.19) * mm});
            skLineSegment(sketch, "E339", {"start": v(-13.74, 5.19) * mm, "end": v(-13.08, 4.9) * mm});
            skLineSegment(sketch, "E340", {"start": v(-13.08, 4.9) * mm, "end": v(-12.9, 4.2) * mm});
            skLineSegment(sketch, "E341", {"start": v(-12.9, 4.2) * mm, "end": v(-12.96, 3.68) * mm});
            skLineSegment(sketch, "E342", {"start": v(-12.96, 3.68) * mm, "end": v(-17.98, 3.68) * mm});
            skLineSegment(sketch, "E343", {"start": v(-17.98, 3.68) * mm, "end": v(-18.45, 0.29) * mm});
            skLineSegment(sketch, "E344", {"start": v(-18.45, 0.29) * mm, "end": v(-13.44, 0.29) * mm});
            skLineSegment(sketch, "E345", {"start": v(-13.44, 0.29) * mm, "end": v(-13.5, -0.25) * mm});
            skLineSegment(sketch, "E346", {"start": v(-13.5, -0.25) * mm, "end": v(-13.9, -0.95) * mm});
            skLineSegment(sketch, "E347", {"start": v(-13.9, -0.95) * mm, "end": v(-14.63, -1.23) * mm});
            skLineSegment(sketch, "E348", {"start": v(-14.63, -1.23) * mm, "end": v(-19.52, -1.23) * mm});
            skLineSegment(sketch, "E349", {"start": v(-6.8, -0.16) * mm, "end": v(-6.8, -0.06) * mm});
            skLineSegment(sketch, "E350", {"start": v(-6.8, -0.06) * mm, "end": v(-6.9, 0.07) * mm});
            skLineSegment(sketch, "E351", {"start": v(-6.9, 0.07) * mm, "end": v(-10.7, 0.07) * mm});
            skLineSegment(sketch, "E352", {"start": v(-10.7, 0.07) * mm, "end": v(-11.01, 0.18) * mm});
            skLineSegment(sketch, "E353", {"start": v(-11.01, 0.18) * mm, "end": v(-10.74, -0.13) * mm});
            skLineSegment(sketch, "E354", {"start": v(-10.74, -0.13) * mm, "end": v(-6.92, -0.13) * mm});
            skLineSegment(sketch, "E355", {"start": v(-6.92, -0.13) * mm, "end": v(-6.8, -0.16) * mm});
            skLineSegment(sketch, "E356", {"start": v(-10.55, 4.94) * mm, "end": v(-10.66, 5.07) * mm});
            skLineSegment(sketch, "E357", {"start": v(-10.66, 5.07) * mm, "end": v(-11.91, 5.07) * mm});
            skLineSegment(sketch, "E358", {"start": v(-11.91, 5.07) * mm, "end": v(-12.05, 4.94) * mm});
            skLineSegment(sketch, "E359", {"start": v(-12.05, 4.94) * mm, "end": v(-12.06, 4.87) * mm});
            skLineSegment(sketch, "E360", {"start": v(-12.06, 4.87) * mm, "end": v(-12.16, 4.2) * mm});
            skLineSegment(sketch, "E361", {"start": v(-12.16, 4.2) * mm, "end": v(-12.08, 4.1) * mm});
            skLineSegment(sketch, "E362", {"start": v(-12.08, 4.1) * mm, "end": v(-12.06, 4.1) * mm});
            skLineSegment(sketch, "E363", {"start": v(-12.06, 4.1) * mm, "end": v(-11.95, 4.2) * mm});
            skLineSegment(sketch, "E364", {"start": v(-11.95, 4.2) * mm, "end": v(-11.86, 4.87) * mm});
            skLineSegment(sketch, "E365", {"start": v(-11.86, 4.87) * mm, "end": v(-10.56, 4.87) * mm});
            skLineSegment(sketch, "E366", {"start": v(-10.56, 4.87) * mm, "end": v(-10.55, 4.94) * mm});
            skLineSegment(sketch, "E367", {"start": v(-10.95, 0.6) * mm, "end": v(-10.67, 0.28) * mm});
            skLineSegment(sketch, "E368", {"start": v(-10.67, 0.28) * mm, "end": v(-6.54, 0.28) * mm});
            skLineSegment(sketch, "E369", {"start": v(-6.54, 0.28) * mm, "end": v(-6.75, -1.23) * mm});
            skLineSegment(sketch, "E370", {"start": v(-6.75, -1.23) * mm, "end": v(-12.79, -1.23) * mm});
            skLineSegment(sketch, "E371", {"start": v(-12.79, -1.23) * mm, "end": v(-13.07, -0.9) * mm});
            skLineSegment(sketch, "E372", {"start": v(-13.07, -0.9) * mm, "end": v(-12.2, 5.27) * mm});
            skLineSegment(sketch, "E373", {"start": v(-12.2, 5.27) * mm, "end": v(-10.3, 5.27) * mm});
            skLineSegment(sketch, "E374", {"start": v(-10.3, 5.27) * mm, "end": v(-10.95, 0.6) * mm});
            skLineSegment(sketch, "E375", {"start": v(0.4, -0.15) * mm, "end": v(0.42, -0.04) * mm});
            skLineSegment(sketch, "E376", {"start": v(0.42, -0.04) * mm, "end": v(0.31, 0.08) * mm});
            skLineSegment(sketch, "E377", {"start": v(0.31, 0.08) * mm, "end": v(-3.91, 0.08) * mm});
            skLineSegment(sketch, "E378", {"start": v(-3.91, 0.08) * mm, "end": v(-4.02, -0.01) * mm});
            skLineSegment(sketch, "E379", {"start": v(-4.02, -0.01) * mm, "end": v(-4.02, -0.03) * mm});
            skLineSegment(sketch, "E380", {"start": v(-4.02, -0.03) * mm, "end": v(-3.94, -0.12) * mm});
            skLineSegment(sketch, "E381", {"start": v(-3.94, -0.12) * mm, "end": v(0.28, -0.12) * mm});
            skLineSegment(sketch, "E382", {"start": v(0.28, -0.12) * mm, "end": v(0.4, -0.15) * mm});
            skLineSegment(sketch, "E383", {"start": v(-1.23, 2.4) * mm, "end": v(-1.21, 2.5) * mm});
            skLineSegment(sketch, "E384", {"start": v(-1.21, 2.5) * mm, "end": v(-1.32, 2.63) * mm});
            skLineSegment(sketch, "E385", {"start": v(-1.32, 2.63) * mm, "end": v(-3.56, 2.63) * mm});
            skLineSegment(sketch, "E386", {"start": v(-3.56, 2.63) * mm, "end": v(-3.66, 2.54) * mm});
            skLineSegment(sketch, "E387", {"start": v(-3.66, 2.54) * mm, "end": v(-3.66, 2.52) * mm});
            skLineSegment(sketch, "E388", {"start": v(-3.66, 2.52) * mm, "end": v(-3.59, 2.42) * mm});
            skLineSegment(sketch, "E389", {"start": v(-3.59, 2.42) * mm, "end": v(-1.35, 2.42) * mm});
            skLineSegment(sketch, "E390", {"start": v(-1.35, 2.42) * mm, "end": v(-1.23, 2.4) * mm});
            skLineSegment(sketch, "E391", {"start": v(-5.18, 4.1) * mm, "end": v(-5.16, 4.1) * mm});
            skLineSegment(sketch, "E392", {"start": v(-5.16, 4.1) * mm, "end": v(-5.06, 4.2) * mm});
            skLineSegment(sketch, "E393", {"start": v(-5.06, 4.2) * mm, "end": v(-4.98, 4.79) * mm});
            skLineSegment(sketch, "E394", {"start": v(-4.98, 4.79) * mm, "end": v(0.97, 4.79) * mm});
            skLineSegment(sketch, "E395", {"start": v(0.97, 4.79) * mm, "end": v(1.1, 4.76) * mm});
            skLineSegment(sketch, "E396", {"start": v(1.1, 4.76) * mm, "end": v(1.1, 4.86) * mm});
            skLineSegment(sketch, "E397", {"start": v(1.1, 4.86) * mm, "end": v(1, 5) * mm});
            skLineSegment(sketch, "E398", {"start": v(1, 5) * mm, "end": v(-5.06, 5) * mm});
            skLineSegment(sketch, "E399", {"start": v(-5.06, 5) * mm, "end": v(-5.16, 4.9) * mm});
            skLineSegment(sketch, "E400", {"start": v(-5.16, 4.9) * mm, "end": v(-5.26, 4.2) * mm});
            skLineSegment(sketch, "E401", {"start": v(-5.26, 4.2) * mm, "end": v(-5.18, 4.1) * mm});
            skLineSegment(sketch, "E402", {"start": v(-6.22, -1.23) * mm, "end": v(-5.32, 5.19) * mm});
            skLineSegment(sketch, "E403", {"start": v(-5.32, 5.19) * mm, "end": v(1.35, 5.19) * mm});
            skLineSegment(sketch, "E404", {"start": v(1.35, 5.19) * mm, "end": v(1.14, 3.67) * mm});
            skLineSegment(sketch, "E405", {"start": v(1.14, 3.67) * mm, "end": v(-3.5, 3.67) * mm});
            skLineSegment(sketch, "E406", {"start": v(-3.5, 3.67) * mm, "end": v(-3.62, 2.83) * mm});
            skLineSegment(sketch, "E407", {"start": v(-3.62, 2.83) * mm, "end": v(-0.97, 2.83) * mm});
            skLineSegment(sketch, "E408", {"start": v(-0.97, 2.83) * mm, "end": v(-1.18, 1.31) * mm});
            skLineSegment(sketch, "E409", {"start": v(-1.18, 1.31) * mm, "end": v(-3.83, 1.31) * mm});
            skLineSegment(sketch, "E410", {"start": v(-3.83, 1.31) * mm, "end": v(-3.98, 0.28) * mm});
            skLineSegment(sketch, "E411", {"start": v(-3.98, 0.28) * mm, "end": v(0.66, 0.28) * mm});
            skLineSegment(sketch, "E412", {"start": v(0.66, 0.28) * mm, "end": v(0.45, -1.23) * mm});
            skLineSegment(sketch, "E413", {"start": v(0.45, -1.23) * mm, "end": v(-6.22, -1.23) * mm});
            skLineSegment(sketch, "E414", {"start": v(4.33, 3.27) * mm, "end": v(3.75, -0.9) * mm});
            skLineSegment(sketch, "E415", {"start": v(3.75, -0.9) * mm, "end": v(3.85, -1.03) * mm});
            skLineSegment(sketch, "E416", {"start": v(3.85, -1.03) * mm, "end": v(3.93, -1.03) * mm});
            skLineSegment(sketch, "E417", {"start": v(3.93, -1.03) * mm, "end": v(3.96, -0.83) * mm});
            skLineSegment(sketch, "E418", {"start": v(3.96, -0.83) * mm, "end": v(4.53, 3.27) * mm});
            skLineSegment(sketch, "E419", {"start": v(4.53, 3.27) * mm, "end": v(4.45, 3.36) * mm});
            skLineSegment(sketch, "E420", {"start": v(4.45, 3.36) * mm, "end": v(4.43, 3.36) * mm});
            skLineSegment(sketch, "E421", {"start": v(4.43, 3.36) * mm, "end": v(4.33, 3.27) * mm});
            skLineSegment(sketch, "E422", {"start": v(2.04, 4.26) * mm, "end": v(2.07, 4.26) * mm});
            skLineSegment(sketch, "E423", {"start": v(2.07, 4.26) * mm, "end": v(2.17, 4.36) * mm});
            skLineSegment(sketch, "E424", {"start": v(2.17, 4.36) * mm, "end": v(2.2, 4.6) * mm});
            skLineSegment(sketch, "E425", {"start": v(2.2, 4.6) * mm, "end": v(2.24, 4.87) * mm});
            skLineSegment(sketch, "E426", {"start": v(2.24, 4.87) * mm, "end": v(8.4, 4.87) * mm});
            skLineSegment(sketch, "E427", {"start": v(8.4, 4.87) * mm, "end": v(8.51, 4.96) * mm});
            skLineSegment(sketch, "E428", {"start": v(8.51, 4.96) * mm, "end": v(8.51, 4.98) * mm});
            skLineSegment(sketch, "E429", {"start": v(8.51, 4.98) * mm, "end": v(8.43, 5.07) * mm});
            skLineSegment(sketch, "E430", {"start": v(8.43, 5.07) * mm, "end": v(2.07, 5.07) * mm});
            skLineSegment(sketch, "E431", {"start": v(2.07, 5.07) * mm, "end": v(1.97, 4.36) * mm});
            skLineSegment(sketch, "E432", {"start": v(1.97, 4.36) * mm, "end": v(2.04, 4.26) * mm});
            skLineSegment(sketch, "E433", {"start": v(1.68, 3.76) * mm, "end": v(1.9, 5.27) * mm});
            skLineSegment(sketch, "E434", {"start": v(1.9, 5.27) * mm, "end": v(8.76, 5.27) * mm});
            skLineSegment(sketch, "E435", {"start": v(8.76, 5.27) * mm, "end": v(8.55, 3.76) * mm});
            skLineSegment(sketch, "E436", {"start": v(8.55, 3.76) * mm, "end": v(6.03, 3.76) * mm});
            skLineSegment(sketch, "E437", {"start": v(6.03, 3.76) * mm, "end": v(5.34, -1.23) * mm});
            skLineSegment(sketch, "E438", {"start": v(5.34, -1.23) * mm, "end": v(3.5, -1.23) * mm});
            skLineSegment(sketch, "E439", {"start": v(3.5, -1.23) * mm, "end": v(4.2, 3.76) * mm});
            skLineSegment(sketch, "E440", {"start": v(4.2, 3.76) * mm, "end": v(1.68, 3.76) * mm});
            skLineSegment(sketch, "E441", {"start": v(15.01, -0.15) * mm, "end": v(15.02, -0.04) * mm});
            skLineSegment(sketch, "E442", {"start": v(15.02, -0.04) * mm, "end": v(14.91, 0.08) * mm});
            skLineSegment(sketch, "E443", {"start": v(14.91, 0.08) * mm, "end": v(10.69, 0.08) * mm});
            skLineSegment(sketch, "E444", {"start": v(10.69, 0.08) * mm, "end": v(10.59, -0.01) * mm});
            skLineSegment(sketch, "E445", {"start": v(10.59, -0.01) * mm, "end": v(10.58, -0.03) * mm});
            skLineSegment(sketch, "E446", {"start": v(10.58, -0.03) * mm, "end": v(10.66, -0.12) * mm});
            skLineSegment(sketch, "E447", {"start": v(10.66, -0.12) * mm, "end": v(14.88, -0.12) * mm});
            skLineSegment(sketch, "E448", {"start": v(14.88, -0.12) * mm, "end": v(15.01, -0.15) * mm});
            skLineSegment(sketch, "E449", {"start": v(13.37, 2.4) * mm, "end": v(13.39, 2.5) * mm});
            skLineSegment(sketch, "E450", {"start": v(13.39, 2.5) * mm, "end": v(13.28, 2.63) * mm});
            skLineSegment(sketch, "E451", {"start": v(13.28, 2.63) * mm, "end": v(11.04, 2.63) * mm});
            skLineSegment(sketch, "E452", {"start": v(11.04, 2.63) * mm, "end": v(10.94, 2.54) * mm});
            skLineSegment(sketch, "E453", {"start": v(10.94, 2.54) * mm, "end": v(10.94, 2.52) * mm});
            skLineSegment(sketch, "E454", {"start": v(10.94, 2.52) * mm, "end": v(11.02, 2.42) * mm});
            skLineSegment(sketch, "E455", {"start": v(11.02, 2.42) * mm, "end": v(13.25, 2.42) * mm});
            skLineSegment(sketch, "E456", {"start": v(13.25, 2.42) * mm, "end": v(13.37, 2.4) * mm});
            skLineSegment(sketch, "E457", {"start": v(9.42, 4.1) * mm, "end": v(9.44, 4.1) * mm});
            skLineSegment(sketch, "E458", {"start": v(9.44, 4.1) * mm, "end": v(9.55, 4.2) * mm});
            skLineSegment(sketch, "E459", {"start": v(9.55, 4.2) * mm, "end": v(9.63, 4.79) * mm});
            skLineSegment(sketch, "E460", {"start": v(9.63, 4.79) * mm, "end": v(15.57, 4.79) * mm});
            skLineSegment(sketch, "E461", {"start": v(15.57, 4.79) * mm, "end": v(15.7, 4.76) * mm});
            skLineSegment(sketch, "E462", {"start": v(15.7, 4.76) * mm, "end": v(15.7, 4.86) * mm});
            skLineSegment(sketch, "E463", {"start": v(15.7, 4.86) * mm, "end": v(15.6, 5) * mm});
            skLineSegment(sketch, "E464", {"start": v(15.6, 5) * mm, "end": v(9.54, 5) * mm});
            skLineSegment(sketch, "E465", {"start": v(9.54, 5) * mm, "end": v(9.44, 4.9) * mm});
            skLineSegment(sketch, "E466", {"start": v(9.44, 4.9) * mm, "end": v(9.34, 4.2) * mm});
            skLineSegment(sketch, "E467", {"start": v(9.34, 4.2) * mm, "end": v(9.42, 4.1) * mm});
            skLineSegment(sketch, "E468", {"start": v(8.38, -1.23) * mm, "end": v(9.28, 5.19) * mm});
            skLineSegment(sketch, "E469", {"start": v(9.28, 5.19) * mm, "end": v(15.95, 5.19) * mm});
            skLineSegment(sketch, "E470", {"start": v(15.95, 5.19) * mm, "end": v(15.74, 3.67) * mm});
            skLineSegment(sketch, "E471", {"start": v(15.74, 3.67) * mm, "end": v(11.1, 3.67) * mm});
            skLineSegment(sketch, "E472", {"start": v(11.1, 3.67) * mm, "end": v(10.98, 2.83) * mm});
            skLineSegment(sketch, "E473", {"start": v(10.98, 2.83) * mm, "end": v(13.63, 2.83) * mm});
            skLineSegment(sketch, "E474", {"start": v(13.63, 2.83) * mm, "end": v(13.42, 1.31) * mm});
            skLineSegment(sketch, "E475", {"start": v(13.42, 1.31) * mm, "end": v(10.77, 1.31) * mm});
            skLineSegment(sketch, "E476", {"start": v(10.77, 1.31) * mm, "end": v(10.63, 0.28) * mm});
            skLineSegment(sketch, "E477", {"start": v(10.63, 0.28) * mm, "end": v(15.27, 0.28) * mm});
            skLineSegment(sketch, "E478", {"start": v(15.27, 0.28) * mm, "end": v(15.06, -1.23) * mm});
            skLineSegment(sketch, "E479", {"start": v(15.06, -1.23) * mm, "end": v(8.38, -1.23) * mm});
            skLineSegment(sketch, "E480", {"start": v(-55.37, -8.12) * mm, "end": v(-54.82, -4.48) * mm});
            skLineSegment(sketch, "E481", {"start": v(-54.82, -4.48) * mm, "end": v(-54.02, -4.48) * mm});
            skLineSegment(sketch, "E482", {"start": v(-54.02, -4.48) * mm, "end": v(-54.57, -8.12) * mm});
            skLineSegment(sketch, "E483", {"start": v(-54.57, -8.12) * mm, "end": v(-55.37, -8.12) * mm});
            skLineSegment(sketch, "E484", {"start": v(-50.95, -8.12) * mm, "end": v(-52.09, -5.37) * mm});
            skLineSegment(sketch, "E485", {"start": v(-52.09, -5.37) * mm, "end": v(-52.47, -8.12) * mm});
            skLineSegment(sketch, "E486", {"start": v(-52.47, -8.12) * mm, "end": v(-53.26, -8.12) * mm});
            skLineSegment(sketch, "E487", {"start": v(-53.26, -8.12) * mm, "end": v(-52.7, -4.48) * mm});
            skLineSegment(sketch, "E488", {"start": v(-52.7, -4.48) * mm, "end": v(-51.74, -4.48) * mm});
            skLineSegment(sketch, "E489", {"start": v(-51.74, -4.48) * mm, "end": v(-50.65, -7.1) * mm});
            skLineSegment(sketch, "E490", {"start": v(-50.65, -7.1) * mm, "end": v(-50.29, -4.48) * mm});
            skLineSegment(sketch, "E491", {"start": v(-50.29, -4.48) * mm, "end": v(-49.52, -4.48) * mm});
            skLineSegment(sketch, "E492", {"start": v(-49.52, -4.48) * mm, "end": v(-50.07, -8.12) * mm});
            skLineSegment(sketch, "E493", {"start": v(-50.07, -8.12) * mm, "end": v(-50.95, -8.12) * mm});
            skLineSegment(sketch, "E494", {"start": v(-45.93, -6.25) * mm, "end": v(-45.9, -6.06) * mm});
            skLineSegment(sketch, "E495", {"start": v(-45.9, -6.06) * mm, "end": v(-45.9, -5.87) * mm});
            skLineSegment(sketch, "E496", {"start": v(-45.9, -5.87) * mm, "end": v(-45.96, -5.43) * mm});
            skLineSegment(sketch, "E497", {"start": v(-45.96, -5.43) * mm, "end": v(-46.23, -5.16) * mm});
            skLineSegment(sketch, "E498", {"start": v(-46.23, -5.16) * mm, "end": v(-46.43, -5.12) * mm});
            skLineSegment(sketch, "E499", {"start": v(-46.43, -5.12) * mm, "end": v(-46.65, -5.11) * mm});
            skLineSegment(sketch, "E500", {"start": v(-46.65, -5.11) * mm, "end": v(-47.53, -5.11) * mm});
            skLineSegment(sketch, "E501", {"start": v(-47.53, -5.11) * mm, "end": v(-47.9, -7.49) * mm});
            skLineSegment(sketch, "E502", {"start": v(-47.9, -7.49) * mm, "end": v(-47, -7.49) * mm});
            skLineSegment(sketch, "E503", {"start": v(-47, -7.49) * mm, "end": v(-46.8, -7.48) * mm});
            skLineSegment(sketch, "E504", {"start": v(-46.8, -7.48) * mm, "end": v(-46.71, -7.47) * mm});
            skLineSegment(sketch, "E505", {"start": v(-46.71, -7.47) * mm, "end": v(-46.62, -7.45) * mm});
            skLineSegment(sketch, "E506", {"start": v(-46.62, -7.45) * mm, "end": v(-46.24, -7.2) * mm});
            skLineSegment(sketch, "E507", {"start": v(-46.24, -7.2) * mm, "end": v(-46.12, -7) * mm});
            skLineSegment(sketch, "E508", {"start": v(-46.12, -7) * mm, "end": v(-46.1, -6.96) * mm});
            skLineSegment(sketch, "E509", {"start": v(-46.1, -6.96) * mm, "end": v(-46.08, -6.88) * mm});
            skLineSegment(sketch, "E510", {"start": v(-46.08, -6.88) * mm, "end": v(-46.01, -6.67) * mm});
            skLineSegment(sketch, "E511", {"start": v(-46.01, -6.67) * mm, "end": v(-45.96, -6.47) * mm});
            skLineSegment(sketch, "E512", {"start": v(-45.96, -6.47) * mm, "end": v(-45.96, -6.45) * mm});
            skLineSegment(sketch, "E513", {"start": v(-45.96, -6.45) * mm, "end": v(-45.94, -6.3) * mm});
            skLineSegment(sketch, "E514", {"start": v(-45.94, -6.3) * mm, "end": v(-45.93, -6.25) * mm});
            skLineSegment(sketch, "E515", {"start": v(-45.08, -6.17) * mm, "end": v(-45.1, -6.28) * mm});
            skLineSegment(sketch, "E516", {"start": v(-45.1, -6.28) * mm, "end": v(-45.1, -6.36) * mm});
            skLineSegment(sketch, "E517", {"start": v(-45.1, -6.36) * mm, "end": v(-45.12, -6.43) * mm});
            skLineSegment(sketch, "E518", {"start": v(-45.12, -6.43) * mm, "end": v(-45.13, -6.5) * mm});
            skLineSegment(sketch, "E519", {"start": v(-45.13, -6.5) * mm, "end": v(-45.16, -6.66) * mm});
            skLineSegment(sketch, "E520", {"start": v(-45.16, -6.66) * mm, "end": v(-45.2, -6.79) * mm});
            skLineSegment(sketch, "E521", {"start": v(-45.2, -6.79) * mm, "end": v(-45.23, -6.93) * mm});
            skLineSegment(sketch, "E522", {"start": v(-45.23, -6.93) * mm, "end": v(-45.28, -7.08) * mm});
            skLineSegment(sketch, "E523", {"start": v(-45.28, -7.08) * mm, "end": v(-45.3, -7.14) * mm});
            skLineSegment(sketch, "E524", {"start": v(-45.3, -7.14) * mm, "end": v(-45.33, -7.2) * mm});
            skLineSegment(sketch, "E525", {"start": v(-45.33, -7.2) * mm, "end": v(-45.4, -7.3) * mm});
            skLineSegment(sketch, "E526", {"start": v(-45.4, -7.3) * mm, "end": v(-45.7, -7.66) * mm});
            skLineSegment(sketch, "E527", {"start": v(-45.7, -7.66) * mm, "end": v(-46.35, -8.03) * mm});
            skLineSegment(sketch, "E528", {"start": v(-46.35, -8.03) * mm, "end": v(-47.07, -8.12) * mm});
            skLineSegment(sketch, "E529", {"start": v(-47.07, -8.12) * mm, "end": v(-48.75, -8.12) * mm});
            skLineSegment(sketch, "E530", {"start": v(-48.75, -8.12) * mm, "end": v(-48.2, -4.48) * mm});
            skLineSegment(sketch, "E531", {"start": v(-48.2, -4.48) * mm, "end": v(-46.54, -4.48) * mm});
            skLineSegment(sketch, "E532", {"start": v(-46.54, -4.48) * mm, "end": v(-45.78, -4.6) * mm});
            skLineSegment(sketch, "E533", {"start": v(-45.78, -4.6) * mm, "end": v(-45.29, -4.98) * mm});
            skLineSegment(sketch, "E534", {"start": v(-45.29, -4.98) * mm, "end": v(-45.06, -6.03) * mm});
            skLineSegment(sketch, "E535", {"start": v(-45.06, -6.03) * mm, "end": v(-45.08, -6.17) * mm});
            skLineSegment(sketch, "E536", {"start": v(-41.27, -5.42) * mm, "end": v(-41.55, -5.13) * mm});
            skLineSegment(sketch, "E537", {"start": v(-41.55, -5.13) * mm, "end": v(-42, -5.04) * mm});
            skLineSegment(sketch, "E538", {"start": v(-42, -5.04) * mm, "end": v(-42.83, -5.42) * mm});
            skLineSegment(sketch, "E539", {"start": v(-42.83, -5.42) * mm, "end": v(-43.16, -6.18) * mm});
            skLineSegment(sketch, "E540", {"start": v(-43.16, -6.18) * mm, "end": v(-43.18, -6.97) * mm});
            skLineSegment(sketch, "E541", {"start": v(-43.18, -6.97) * mm, "end": v(-43.1, -7.27) * mm});
            skLineSegment(sketch, "E542", {"start": v(-43.1, -7.27) * mm, "end": v(-42.86, -7.47) * mm});
            skLineSegment(sketch, "E543", {"start": v(-42.86, -7.47) * mm, "end": v(-42.62, -7.54) * mm});
            skLineSegment(sketch, "E544", {"start": v(-42.62, -7.54) * mm, "end": v(-42.16, -7.57) * mm});
            skLineSegment(sketch, "E545", {"start": v(-42.16, -7.57) * mm, "end": v(-41.54, -7.2) * mm});
            skLineSegment(sketch, "E546", {"start": v(-41.54, -7.2) * mm, "end": v(-41.2, -6.3) * mm});
            skLineSegment(sketch, "E547", {"start": v(-41.2, -6.3) * mm, "end": v(-41.27, -5.42) * mm});
            skLineSegment(sketch, "E548", {"start": v(-41.03, -7.72) * mm, "end": v(-41.64, -8.07) * mm});
            skLineSegment(sketch, "E549", {"start": v(-41.64, -8.07) * mm, "end": v(-42.48, -8.2) * mm});
            skLineSegment(sketch, "E550", {"start": v(-42.48, -8.2) * mm, "end": v(-43.26, -8.07) * mm});
            skLineSegment(sketch, "E551", {"start": v(-43.26, -8.07) * mm, "end": v(-43.78, -7.71) * mm});
            skLineSegment(sketch, "E552", {"start": v(-43.78, -7.71) * mm, "end": v(-44.02, -7.12) * mm});
            skLineSegment(sketch, "E553", {"start": v(-44.02, -7.12) * mm, "end": v(-44, -6.3) * mm});
            skLineSegment(sketch, "E554", {"start": v(-44, -6.3) * mm, "end": v(-43.77, -5.48) * mm});
            skLineSegment(sketch, "E555", {"start": v(-43.77, -5.48) * mm, "end": v(-43.35, -4.9) * mm});
            skLineSegment(sketch, "E556", {"start": v(-43.35, -4.9) * mm, "end": v(-42.76, -4.53) * mm});
            skLineSegment(sketch, "E557", {"start": v(-42.76, -4.53) * mm, "end": v(-42.04, -4.41) * mm});
            skLineSegment(sketch, "E558", {"start": v(-42.04, -4.41) * mm, "end": v(-40.88, -4.64) * mm});
            skLineSegment(sketch, "E559", {"start": v(-40.88, -4.64) * mm, "end": v(-40.36, -5.5) * mm});
            skLineSegment(sketch, "E560", {"start": v(-40.36, -5.5) * mm, "end": v(-40.34, -5.96) * mm});
            skLineSegment(sketch, "E561", {"start": v(-40.34, -5.96) * mm, "end": v(-40.4, -6.56) * mm});
            skLineSegment(sketch, "E562", {"start": v(-40.4, -6.56) * mm, "end": v(-41.03, -7.72) * mm});
            skLineSegment(sketch, "E563", {"start": v(-36.55, -5.42) * mm, "end": v(-36.83, -5.13) * mm});
            skLineSegment(sketch, "E564", {"start": v(-36.83, -5.13) * mm, "end": v(-37.28, -5.04) * mm});
            skLineSegment(sketch, "E565", {"start": v(-37.28, -5.04) * mm, "end": v(-38.11, -5.42) * mm});
            skLineSegment(sketch, "E566", {"start": v(-38.11, -5.42) * mm, "end": v(-38.44, -6.18) * mm});
            skLineSegment(sketch, "E567", {"start": v(-38.44, -6.18) * mm, "end": v(-38.46, -6.97) * mm});
            skLineSegment(sketch, "E568", {"start": v(-38.46, -6.97) * mm, "end": v(-38.38, -7.27) * mm});
            skLineSegment(sketch, "E569", {"start": v(-38.38, -7.27) * mm, "end": v(-38.14, -7.47) * mm});
            skLineSegment(sketch, "E570", {"start": v(-38.14, -7.47) * mm, "end": v(-37.9, -7.54) * mm});
            skLineSegment(sketch, "E571", {"start": v(-37.9, -7.54) * mm, "end": v(-37.44, -7.57) * mm});
            skLineSegment(sketch, "E572", {"start": v(-37.44, -7.57) * mm, "end": v(-36.82, -7.2) * mm});
            skLineSegment(sketch, "E573", {"start": v(-36.82, -7.2) * mm, "end": v(-36.48, -6.3) * mm});
            skLineSegment(sketch, "E574", {"start": v(-36.48, -6.3) * mm, "end": v(-36.55, -5.42) * mm});
            skLineSegment(sketch, "E575", {"start": v(-36.31, -7.72) * mm, "end": v(-36.93, -8.07) * mm});
            skLineSegment(sketch, "E576", {"start": v(-36.93, -8.07) * mm, "end": v(-37.76, -8.2) * mm});
            skLineSegment(sketch, "E577", {"start": v(-37.76, -8.2) * mm, "end": v(-38.54, -8.07) * mm});
            skLineSegment(sketch, "E578", {"start": v(-38.54, -8.07) * mm, "end": v(-39.06, -7.71) * mm});
            skLineSegment(sketch, "E579", {"start": v(-39.06, -7.71) * mm, "end": v(-39.3, -7.12) * mm});
            skLineSegment(sketch, "E580", {"start": v(-39.3, -7.12) * mm, "end": v(-39.29, -6.3) * mm});
            skLineSegment(sketch, "E581", {"start": v(-39.29, -6.3) * mm, "end": v(-39.05, -5.48) * mm});
            skLineSegment(sketch, "E582", {"start": v(-39.05, -5.48) * mm, "end": v(-38.63, -4.9) * mm});
            skLineSegment(sketch, "E583", {"start": v(-38.63, -4.9) * mm, "end": v(-38.05, -4.53) * mm});
            skLineSegment(sketch, "E584", {"start": v(-38.05, -4.53) * mm, "end": v(-37.32, -4.41) * mm});
            skLineSegment(sketch, "E585", {"start": v(-37.32, -4.41) * mm, "end": v(-36.16, -4.64) * mm});
            skLineSegment(sketch, "E586", {"start": v(-36.16, -4.64) * mm, "end": v(-35.64, -5.5) * mm});
            skLineSegment(sketch, "E587", {"start": v(-35.64, -5.5) * mm, "end": v(-35.63, -5.96) * mm});
            skLineSegment(sketch, "E588", {"start": v(-35.63, -5.96) * mm, "end": v(-35.69, -6.56) * mm});
            skLineSegment(sketch, "E589", {"start": v(-35.69, -6.56) * mm, "end": v(-36.31, -7.72) * mm});
            skLineSegment(sketch, "E590", {"start": v(-31.91, -5.26) * mm, "end": v(-32.46, -5.13) * mm});
            skLineSegment(sketch, "E591", {"start": v(-32.46, -5.13) * mm, "end": v(-33.4, -5.13) * mm});
            skLineSegment(sketch, "E592", {"start": v(-33.4, -5.13) * mm, "end": v(-33.53, -6.05) * mm});
            skLineSegment(sketch, "E593", {"start": v(-33.53, -6.05) * mm, "end": v(-32.6, -6.05) * mm});
            skLineSegment(sketch, "E594", {"start": v(-32.6, -6.05) * mm, "end": v(-32.03, -5.93) * mm});
            skLineSegment(sketch, "E595", {"start": v(-32.03, -5.93) * mm, "end": v(-31.84, -5.59) * mm});
            skLineSegment(sketch, "E596", {"start": v(-31.84, -5.59) * mm, "end": v(-31.91, -5.26) * mm});
            skLineSegment(sketch, "E597", {"start": v(-32.14, -8.12) * mm, "end": v(-32.73, -6.7) * mm});
            skLineSegment(sketch, "E598", {"start": v(-32.73, -6.7) * mm, "end": v(-33.63, -6.7) * mm});
            skLineSegment(sketch, "E599", {"start": v(-33.63, -6.7) * mm, "end": v(-33.84, -8.12) * mm});
            skLineSegment(sketch, "E600", {"start": v(-33.84, -8.12) * mm, "end": v(-34.6, -8.12) * mm});
            skLineSegment(sketch, "E601", {"start": v(-34.6, -8.12) * mm, "end": v(-34.06, -4.48) * mm});
            skLineSegment(sketch, "E602", {"start": v(-34.06, -4.48) * mm, "end": v(-32, -4.48) * mm});
            skLineSegment(sketch, "E603", {"start": v(-32, -4.48) * mm, "end": v(-31.86, -4.5) * mm});
            skLineSegment(sketch, "E604", {"start": v(-31.86, -4.5) * mm, "end": v(-31.75, -4.52) * mm});
            skLineSegment(sketch, "E605", {"start": v(-31.75, -4.52) * mm, "end": v(-31.69, -4.53) * mm});
            skLineSegment(sketch, "E606", {"start": v(-31.69, -4.53) * mm, "end": v(-31.57, -4.56) * mm});
            skLineSegment(sketch, "E607", {"start": v(-31.57, -4.56) * mm, "end": v(-31.13, -4.95) * mm});
            skLineSegment(sketch, "E608", {"start": v(-31.13, -4.95) * mm, "end": v(-31.08, -5.6) * mm});
            skLineSegment(sketch, "E609", {"start": v(-31.08, -5.6) * mm, "end": v(-31.35, -6.24) * mm});
            skLineSegment(sketch, "E610", {"start": v(-31.35, -6.24) * mm, "end": v(-31.96, -6.6) * mm});
            skLineSegment(sketch, "E611", {"start": v(-31.96, -6.6) * mm, "end": v(-31.3, -8.12) * mm});
            skLineSegment(sketch, "E612", {"start": v(-31.3, -8.12) * mm, "end": v(-32.14, -8.12) * mm});
            skLineSegment(sketch, "E613", {"start": v(-24.77, -7.88) * mm, "end": v(-25.69, -8.06) * mm});
            skLineSegment(sketch, "E614", {"start": v(-25.69, -8.06) * mm, "end": v(-27.76, -8.12) * mm});
            skLineSegment(sketch, "E615", {"start": v(-27.76, -8.12) * mm, "end": v(-27.66, -7.47) * mm});
            skLineSegment(sketch, "E616", {"start": v(-27.66, -7.47) * mm, "end": v(-25.75, -7.47) * mm});
            skLineSegment(sketch, "E617", {"start": v(-25.75, -7.47) * mm, "end": v(-25.33, -7.4) * mm});
            skLineSegment(sketch, "E618", {"start": v(-25.33, -7.4) * mm, "end": v(-25.1, -7.15) * mm});
            skLineSegment(sketch, "E619", {"start": v(-25.1, -7.15) * mm, "end": v(-25.09, -6.92) * mm});
            skLineSegment(sketch, "E620", {"start": v(-25.09, -6.92) * mm, "end": v(-25.1, -6.83) * mm});
            skLineSegment(sketch, "E621", {"start": v(-25.1, -6.83) * mm, "end": v(-25.13, -6.76) * mm});
            skLineSegment(sketch, "E622", {"start": v(-25.13, -6.76) * mm, "end": v(-25.86, -6.63) * mm});
            skLineSegment(sketch, "E623", {"start": v(-25.86, -6.63) * mm, "end": v(-26.03, -6.63) * mm});
            skLineSegment(sketch, "E624", {"start": v(-26.03, -6.63) * mm, "end": v(-26.28, -6.64) * mm});
            skLineSegment(sketch, "E625", {"start": v(-26.28, -6.64) * mm, "end": v(-27.1, -6.54) * mm});
            skLineSegment(sketch, "E626", {"start": v(-27.1, -6.54) * mm, "end": v(-27.48, -6.2) * mm});
            skLineSegment(sketch, "E627", {"start": v(-27.48, -6.2) * mm, "end": v(-27.54, -5.65) * mm});
            skLineSegment(sketch, "E628", {"start": v(-27.54, -5.65) * mm, "end": v(-27.04, -4.72) * mm});
            skLineSegment(sketch, "E629", {"start": v(-27.04, -4.72) * mm, "end": v(-26.08, -4.48) * mm});
            skLineSegment(sketch, "E630", {"start": v(-26.08, -4.48) * mm, "end": v(-24.08, -4.48) * mm});
            skLineSegment(sketch, "E631", {"start": v(-24.08, -4.48) * mm, "end": v(-24.17, -5.13) * mm});
            skLineSegment(sketch, "E632", {"start": v(-24.17, -5.13) * mm, "end": v(-26.06, -5.13) * mm});
            skLineSegment(sketch, "E633", {"start": v(-26.06, -5.13) * mm, "end": v(-26.51, -5.24) * mm});
            skLineSegment(sketch, "E634", {"start": v(-26.51, -5.24) * mm, "end": v(-26.73, -5.58) * mm});
            skLineSegment(sketch, "E635", {"start": v(-26.73, -5.58) * mm, "end": v(-26.64, -5.9) * mm});
            skLineSegment(sketch, "E636", {"start": v(-26.64, -5.9) * mm, "end": v(-26.24, -5.98) * mm});
            skLineSegment(sketch, "E637", {"start": v(-26.24, -5.98) * mm, "end": v(-25.3, -6) * mm});
            skLineSegment(sketch, "E638", {"start": v(-25.3, -6) * mm, "end": v(-25, -6) * mm});
            skLineSegment(sketch, "E639", {"start": v(-25, -6) * mm, "end": v(-24.9, -6.02) * mm});
            skLineSegment(sketch, "E640", {"start": v(-24.9, -6.02) * mm, "end": v(-24.79, -6.04) * mm});
            skLineSegment(sketch, "E641", {"start": v(-24.79, -6.04) * mm, "end": v(-24.57, -6.13) * mm});
            skLineSegment(sketch, "E642", {"start": v(-24.57, -6.13) * mm, "end": v(-24.5, -6.2) * mm});
            skLineSegment(sketch, "E643", {"start": v(-24.5, -6.2) * mm, "end": v(-24.4, -6.3) * mm});
            skLineSegment(sketch, "E644", {"start": v(-24.4, -6.3) * mm, "end": v(-24.27, -6.62) * mm});
            skLineSegment(sketch, "E645", {"start": v(-24.27, -6.62) * mm, "end": v(-24.31, -7.21) * mm});
            skLineSegment(sketch, "E646", {"start": v(-24.31, -7.21) * mm, "end": v(-24.77, -7.88) * mm});
            skLineSegment(sketch, "E647", {"start": v(-20.92, -8.12) * mm, "end": v(-22.03, -6.31) * mm});
            skLineSegment(sketch, "E648", {"start": v(-22.03, -6.31) * mm, "end": v(-22.3, -8.12) * mm});
            skLineSegment(sketch, "E649", {"start": v(-22.3, -8.12) * mm, "end": v(-23.07, -8.12) * mm});
            skLineSegment(sketch, "E650", {"start": v(-23.07, -8.12) * mm, "end": v(-22.52, -4.48) * mm});
            skLineSegment(sketch, "E651", {"start": v(-22.52, -4.48) * mm, "end": v(-21.75, -4.48) * mm});
            skLineSegment(sketch, "E652", {"start": v(-21.75, -4.48) * mm, "end": v(-22.02, -6.23) * mm});
            skLineSegment(sketch, "E653", {"start": v(-22.02, -6.23) * mm, "end": v(-20.32, -4.48) * mm});
            skLineSegment(sketch, "E654", {"start": v(-20.32, -4.48) * mm, "end": v(-19.4, -4.48) * mm});
            skLineSegment(sketch, "E655", {"start": v(-19.4, -4.48) * mm, "end": v(-21.14, -6.26) * mm});
            skLineSegment(sketch, "E656", {"start": v(-21.14, -6.26) * mm, "end": v(-19.95, -8.12) * mm});
            skLineSegment(sketch, "E657", {"start": v(-19.95, -8.12) * mm, "end": v(-20.92, -8.12) * mm});
            skLineSegment(sketch, "E658", {"start": v(-17.05, -6.52) * mm, "end": v(-17.29, -8.12) * mm});
            skLineSegment(sketch, "E659", {"start": v(-17.29, -8.12) * mm, "end": v(-18.06, -8.12) * mm});
            skLineSegment(sketch, "E660", {"start": v(-18.06, -8.12) * mm, "end": v(-17.82, -6.52) * mm});
            skLineSegment(sketch, "E661", {"start": v(-17.82, -6.52) * mm, "end": v(-18.88, -4.48) * mm});
            skLineSegment(sketch, "E662", {"start": v(-18.88, -4.48) * mm, "end": v(-18.03, -4.48) * mm});
            skLineSegment(sketch, "E663", {"start": v(-18.03, -4.48) * mm, "end": v(-17.34, -5.88) * mm});
            skLineSegment(sketch, "E664", {"start": v(-17.34, -5.88) * mm, "end": v(-16.23, -4.48) * mm});
            skLineSegment(sketch, "E665", {"start": v(-16.23, -4.48) * mm, "end": v(-15.35, -4.48) * mm});
            skLineSegment(sketch, "E666", {"start": v(-15.35, -4.48) * mm, "end": v(-17.05, -6.52) * mm});
            skLineSegment(sketch, "E667", {"start": v(-12.1, -6.25) * mm, "end": v(-12.08, -6.06) * mm});
            skLineSegment(sketch, "E668", {"start": v(-12.08, -6.06) * mm, "end": v(-12.07, -5.87) * mm});
            skLineSegment(sketch, "E669", {"start": v(-12.07, -5.87) * mm, "end": v(-12.13, -5.43) * mm});
            skLineSegment(sketch, "E670", {"start": v(-12.13, -5.43) * mm, "end": v(-12.4, -5.16) * mm});
            skLineSegment(sketch, "E671", {"start": v(-12.4, -5.16) * mm, "end": v(-12.6, -5.12) * mm});
            skLineSegment(sketch, "E672", {"start": v(-12.6, -5.12) * mm, "end": v(-12.82, -5.11) * mm});
            skLineSegment(sketch, "E673", {"start": v(-12.82, -5.11) * mm, "end": v(-13.7, -5.11) * mm});
            skLineSegment(sketch, "E674", {"start": v(-13.7, -5.11) * mm, "end": v(-14.06, -7.49) * mm});
            skLineSegment(sketch, "E675", {"start": v(-14.06, -7.49) * mm, "end": v(-13.18, -7.49) * mm});
            skLineSegment(sketch, "E676", {"start": v(-13.18, -7.49) * mm, "end": v(-12.97, -7.48) * mm});
            skLineSegment(sketch, "E677", {"start": v(-12.97, -7.48) * mm, "end": v(-12.88, -7.47) * mm});
            skLineSegment(sketch, "E678", {"start": v(-12.88, -7.47) * mm, "end": v(-12.8, -7.45) * mm});
            skLineSegment(sketch, "E679", {"start": v(-12.8, -7.45) * mm, "end": v(-12.4, -7.2) * mm});
            skLineSegment(sketch, "E680", {"start": v(-12.4, -7.2) * mm, "end": v(-12.3, -7) * mm});
            skLineSegment(sketch, "E681", {"start": v(-12.3, -7) * mm, "end": v(-12.28, -6.96) * mm});
            skLineSegment(sketch, "E682", {"start": v(-12.28, -6.96) * mm, "end": v(-12.25, -6.88) * mm});
            skLineSegment(sketch, "E683", {"start": v(-12.25, -6.88) * mm, "end": v(-12.18, -6.67) * mm});
            skLineSegment(sketch, "E684", {"start": v(-12.18, -6.67) * mm, "end": v(-12.13, -6.47) * mm});
            skLineSegment(sketch, "E685", {"start": v(-12.13, -6.47) * mm, "end": v(-12.13, -6.45) * mm});
            skLineSegment(sketch, "E686", {"start": v(-12.13, -6.45) * mm, "end": v(-12.1, -6.3) * mm});
            skLineSegment(sketch, "E687", {"start": v(-12.1, -6.3) * mm, "end": v(-12.1, -6.25) * mm});
            skLineSegment(sketch, "E688", {"start": v(-11.25, -6.17) * mm, "end": v(-11.27, -6.28) * mm});
            skLineSegment(sketch, "E689", {"start": v(-11.27, -6.28) * mm, "end": v(-11.28, -6.36) * mm});
            skLineSegment(sketch, "E690", {"start": v(-11.28, -6.36) * mm, "end": v(-11.29, -6.43) * mm});
            skLineSegment(sketch, "E691", {"start": v(-11.29, -6.43) * mm, "end": v(-11.3, -6.5) * mm});
            skLineSegment(sketch, "E692", {"start": v(-11.3, -6.5) * mm, "end": v(-11.33, -6.66) * mm});
            skLineSegment(sketch, "E693", {"start": v(-11.33, -6.66) * mm, "end": v(-11.37, -6.79) * mm});
            skLineSegment(sketch, "E694", {"start": v(-11.37, -6.79) * mm, "end": v(-11.4, -6.93) * mm});
            skLineSegment(sketch, "E695", {"start": v(-11.4, -6.93) * mm, "end": v(-11.45, -7.08) * mm});
            skLineSegment(sketch, "E696", {"start": v(-11.45, -7.08) * mm, "end": v(-11.48, -7.14) * mm});
            skLineSegment(sketch, "E697", {"start": v(-11.48, -7.14) * mm, "end": v(-11.5, -7.2) * mm});
            skLineSegment(sketch, "E698", {"start": v(-11.5, -7.2) * mm, "end": v(-11.56, -7.3) * mm});
            skLineSegment(sketch, "E699", {"start": v(-11.56, -7.3) * mm, "end": v(-11.87, -7.66) * mm});
            skLineSegment(sketch, "E700", {"start": v(-11.87, -7.66) * mm, "end": v(-12.52, -8.03) * mm});
            skLineSegment(sketch, "E701", {"start": v(-12.52, -8.03) * mm, "end": v(-13.24, -8.12) * mm});
            skLineSegment(sketch, "E702", {"start": v(-13.24, -8.12) * mm, "end": v(-14.92, -8.12) * mm});
            skLineSegment(sketch, "E703", {"start": v(-14.92, -8.12) * mm, "end": v(-14.37, -4.48) * mm});
            skLineSegment(sketch, "E704", {"start": v(-14.37, -4.48) * mm, "end": v(-12.71, -4.48) * mm});
            skLineSegment(sketch, "E705", {"start": v(-12.71, -4.48) * mm, "end": v(-11.95, -4.6) * mm});
            skLineSegment(sketch, "E706", {"start": v(-11.95, -4.6) * mm, "end": v(-11.46, -4.98) * mm});
            skLineSegment(sketch, "E707", {"start": v(-11.46, -4.98) * mm, "end": v(-11.23, -6.03) * mm});
            skLineSegment(sketch, "E708", {"start": v(-11.23, -6.03) * mm, "end": v(-11.25, -6.17) * mm});
            skLineSegment(sketch, "E709", {"start": v(-10.21, -8.12) * mm, "end": v(-9.66, -4.48) * mm});
            skLineSegment(sketch, "E710", {"start": v(-9.66, -4.48) * mm, "end": v(-8.87, -4.48) * mm});
            skLineSegment(sketch, "E711", {"start": v(-8.87, -4.48) * mm, "end": v(-9.41, -8.12) * mm});
            skLineSegment(sketch, "E712", {"start": v(-9.41, -8.12) * mm, "end": v(-10.21, -8.12) * mm});
            skLineSegment(sketch, "E713", {"start": v(-6, -8.12) * mm, "end": v(-6.8, -8.12) * mm});
            skLineSegment(sketch, "E714", {"start": v(-6.8, -8.12) * mm, "end": v(-7.82, -4.48) * mm});
            skLineSegment(sketch, "E715", {"start": v(-7.82, -4.48) * mm, "end": v(-6.96, -4.48) * mm});
            skLineSegment(sketch, "E716", {"start": v(-6.96, -4.48) * mm, "end": v(-6.28, -7.19) * mm});
            skLineSegment(sketch, "E717", {"start": v(-6.28, -7.19) * mm, "end": v(-4.75, -4.48) * mm});
            skLineSegment(sketch, "E718", {"start": v(-4.75, -4.48) * mm, "end": v(-3.94, -4.48) * mm});
            skLineSegment(sketch, "E719", {"start": v(-3.94, -4.48) * mm, "end": v(-6, -8.12) * mm});
            skLineSegment(sketch, "E720", {"start": v(-3.49, -8.12) * mm, "end": v(-2.94, -4.48) * mm});
            skLineSegment(sketch, "E721", {"start": v(-2.94, -4.48) * mm, "end": v(-2.14, -4.48) * mm});
            skLineSegment(sketch, "E722", {"start": v(-2.14, -4.48) * mm, "end": v(-2.69, -8.12) * mm});
            skLineSegment(sketch, "E723", {"start": v(-2.69, -8.12) * mm, "end": v(-3.49, -8.12) * mm});
            skLineSegment(sketch, "E724", {"start": v(0.94, -8.12) * mm, "end": v(-0.2, -5.37) * mm});
            skLineSegment(sketch, "E725", {"start": v(-0.2, -5.37) * mm, "end": v(-0.6, -8.12) * mm});
            skLineSegment(sketch, "E726", {"start": v(-0.6, -8.12) * mm, "end": v(-1.37, -8.12) * mm});
            skLineSegment(sketch, "E727", {"start": v(-1.37, -8.12) * mm, "end": v(-0.83, -4.48) * mm});
            skLineSegment(sketch, "E728", {"start": v(-0.83, -4.48) * mm, "end": v(0.15, -4.48) * mm});
            skLineSegment(sketch, "E729", {"start": v(0.15, -4.48) * mm, "end": v(1.23, -7.1) * mm});
            skLineSegment(sketch, "E730", {"start": v(1.23, -7.1) * mm, "end": v(1.6, -4.48) * mm});
            skLineSegment(sketch, "E731", {"start": v(1.6, -4.48) * mm, "end": v(2.37, -4.48) * mm});
            skLineSegment(sketch, "E732", {"start": v(2.37, -4.48) * mm, "end": v(1.82, -8.12) * mm});
            skLineSegment(sketch, "E733", {"start": v(1.82, -8.12) * mm, "end": v(0.94, -8.12) * mm});
            skLineSegment(sketch, "E734", {"start": v(4.55, -8.12) * mm, "end": v(4.43, -8.11) * mm});
            skLineSegment(sketch, "E735", {"start": v(4.43, -8.11) * mm, "end": v(4.42, -8.1) * mm});
            skLineSegment(sketch, "E736", {"start": v(4.42, -8.1) * mm, "end": v(4.28, -8.08) * mm});
            skLineSegment(sketch, "E737", {"start": v(4.28, -8.08) * mm, "end": v(4.01, -7.99) * mm});
            skLineSegment(sketch, "E738", {"start": v(4.01, -7.99) * mm, "end": v(3.83, -7.87) * mm});
            skLineSegment(sketch, "E739", {"start": v(3.83, -7.87) * mm, "end": v(3.67, -7.73) * mm});
            skLineSegment(sketch, "E740", {"start": v(3.67, -7.73) * mm, "end": v(3.38, -7.1) * mm});
            skLineSegment(sketch, "E741", {"start": v(3.38, -7.1) * mm, "end": v(3.4, -6.25) * mm});
            skLineSegment(sketch, "E742", {"start": v(3.4, -6.25) * mm, "end": v(3.72, -5.35) * mm});
            skLineSegment(sketch, "E743", {"start": v(3.72, -5.35) * mm, "end": v(4.53, -4.62) * mm});
            skLineSegment(sketch, "E744", {"start": v(4.53, -4.62) * mm, "end": v(4.93, -4.51) * mm});
            skLineSegment(sketch, "E745", {"start": v(4.93, -4.51) * mm, "end": v(5.58, -4.49) * mm});
            skLineSegment(sketch, "E746", {"start": v(5.58, -4.49) * mm, "end": v(7.03, -4.48) * mm});
            skLineSegment(sketch, "E747", {"start": v(7.03, -4.48) * mm, "end": v(6.94, -5.11) * mm});
            skLineSegment(sketch, "E748", {"start": v(6.94, -5.11) * mm, "end": v(5.3, -5.11) * mm});
            skLineSegment(sketch, "E749", {"start": v(5.3, -5.11) * mm, "end": v(4.55, -5.47) * mm});
            skLineSegment(sketch, "E750", {"start": v(4.55, -5.47) * mm, "end": v(4.28, -6.2) * mm});
            skLineSegment(sketch, "E751", {"start": v(4.28, -6.2) * mm, "end": v(4.23, -6.58) * mm});
            skLineSegment(sketch, "E752", {"start": v(4.23, -6.58) * mm, "end": v(4.23, -6.7) * mm});
            skLineSegment(sketch, "E753", {"start": v(4.23, -6.7) * mm, "end": v(4.23, -6.71) * mm});
            skLineSegment(sketch, "E754", {"start": v(4.23, -6.71) * mm, "end": v(4.23, -6.86) * mm});
            skLineSegment(sketch, "E755", {"start": v(4.23, -6.86) * mm, "end": v(4.42, -7.3) * mm});
            skLineSegment(sketch, "E756", {"start": v(4.42, -7.3) * mm, "end": v(4.85, -7.41) * mm});
            skLineSegment(sketch, "E757", {"start": v(4.85, -7.41) * mm, "end": v(5.8, -7.45) * mm});
            skLineSegment(sketch, "E758", {"start": v(5.8, -7.45) * mm, "end": v(5.93, -6.6) * mm});
            skLineSegment(sketch, "E759", {"start": v(5.93, -6.6) * mm, "end": v(4.92, -6.6) * mm});
            skLineSegment(sketch, "E760", {"start": v(4.92, -6.6) * mm, "end": v(5.01, -5.96) * mm});
            skLineSegment(sketch, "E761", {"start": v(5.01, -5.96) * mm, "end": v(6.8, -5.96) * mm});
            skLineSegment(sketch, "E762", {"start": v(6.8, -5.96) * mm, "end": v(6.48, -8.12) * mm});
            skLineSegment(sketch, "E763", {"start": v(6.48, -8.12) * mm, "end": v(4.55, -8.12) * mm});
            skLineSegment(sketch, "E764", {"start": v(44.76, -7.62) * mm, "end": v(44.3, -8.1) * mm});
            skLineSegment(sketch, "E765", {"start": v(44.3, -8.1) * mm, "end": v(43.78, -8.4) * mm});
            skLineSegment(sketch, "E766", {"start": v(43.78, -8.4) * mm, "end": v(43.24, -8.48) * mm});
            skLineSegment(sketch, "E767", {"start": v(43.24, -8.48) * mm, "end": v(42.75, -8.32) * mm});
            skLineSegment(sketch, "E768", {"start": v(42.75, -8.32) * mm, "end": v(42.42, -7.93) * mm});
            skLineSegment(sketch, "E769", {"start": v(42.42, -7.93) * mm, "end": v(42.28, -7.4) * mm});
            skLineSegment(sketch, "E770", {"start": v(42.28, -7.4) * mm, "end": v(42.36, -6.8) * mm});
            skLineSegment(sketch, "E771", {"start": v(42.36, -6.8) * mm, "end": v(42.65, -6.2) * mm});
            skLineSegment(sketch, "E772", {"start": v(42.65, -6.2) * mm, "end": v(43.1, -5.7) * mm});
            skLineSegment(sketch, "E773", {"start": v(43.1, -5.7) * mm, "end": v(43.63, -5.4) * mm});
            skLineSegment(sketch, "E774", {"start": v(43.63, -5.4) * mm, "end": v(44.17, -5.33) * mm});
            skLineSegment(sketch, "E775", {"start": v(44.17, -5.33) * mm, "end": v(44.65, -5.5) * mm});
            skLineSegment(sketch, "E776", {"start": v(44.65, -5.5) * mm, "end": v(45, -5.88) * mm});
            skLineSegment(sketch, "E777", {"start": v(45, -5.88) * mm, "end": v(45.12, -6.4) * mm});
            skLineSegment(sketch, "E778", {"start": v(45.12, -6.4) * mm, "end": v(45.05, -7) * mm});
            skLineSegment(sketch, "E779", {"start": v(45.05, -7) * mm, "end": v(44.76, -7.62) * mm});
            skLineSegment(sketch, "E780", {"start": v(54.43, -5.42) * mm, "end": v(53.97, -5.65) * mm});
            skLineSegment(sketch, "E781", {"start": v(53.97, -5.65) * mm, "end": v(53.67, -5.8) * mm});
            skLineSegment(sketch, "E782", {"start": v(53.67, -5.8) * mm, "end": v(53.33, -5.96) * mm});
            skLineSegment(sketch, "E783", {"start": v(53.33, -5.96) * mm, "end": v(52.55, -6.34) * mm});
            skLineSegment(sketch, "E784", {"start": v(52.55, -6.34) * mm, "end": v(51.62, -6.77) * mm});
            skLineSegment(sketch, "E785", {"start": v(51.62, -6.77) * mm, "end": v(51.1, -7) * mm});
            skLineSegment(sketch, "E786", {"start": v(51.1, -7) * mm, "end": v(50.56, -7.23) * mm});
            skLineSegment(sketch, "E787", {"start": v(50.56, -7.23) * mm, "end": v(49.98, -7.48) * mm});
            skLineSegment(sketch, "E788", {"start": v(49.98, -7.48) * mm, "end": v(49.37, -7.73) * mm});
            skLineSegment(sketch, "E789", {"start": v(49.37, -7.73) * mm, "end": v(48.73, -7.98) * mm});
            skLineSegment(sketch, "E790", {"start": v(48.73, -7.98) * mm, "end": v(48.07, -8.23) * mm});
            skLineSegment(sketch, "E791", {"start": v(48.07, -8.23) * mm, "end": v(47.38, -8.48) * mm});
            skLineSegment(sketch, "E792", {"start": v(47.38, -8.48) * mm, "end": v(46.67, -8.72) * mm});
            skLineSegment(sketch, "E793", {"start": v(46.67, -8.72) * mm, "end": v(43.6, -9.65) * mm});
            skLineSegment(sketch, "E794", {"start": v(43.6, -9.65) * mm, "end": v(42.8, -9.85) * mm});
            skLineSegment(sketch, "E795", {"start": v(42.8, -9.85) * mm, "end": v(41.97, -10.04) * mm});
            skLineSegment(sketch, "E796", {"start": v(41.97, -10.04) * mm, "end": v(41.13, -10.22) * mm});
            skLineSegment(sketch, "E797", {"start": v(41.13, -10.22) * mm, "end": v(40.28, -10.38) * mm});
            skLineSegment(sketch, "E798", {"start": v(40.28, -10.38) * mm, "end": v(39.96, -10.43) * mm});
            skLineSegment(sketch, "E799", {"start": v(39.96, -10.43) * mm, "end": v(40.15, -10.05) * mm});
            skLineSegment(sketch, "E800", {"start": v(40.15, -10.05) * mm, "end": v(40.55, -9.04) * mm});
            skLineSegment(sketch, "E801", {"start": v(40.55, -9.04) * mm, "end": v(40.86, -8.05) * mm});
            skLineSegment(sketch, "E802", {"start": v(40.86, -8.05) * mm, "end": v(41.2, -6.2) * mm});
            skLineSegment(sketch, "E803", {"start": v(41.2, -6.2) * mm, "end": v(41.28, -4.63) * mm});
            skLineSegment(sketch, "E804", {"start": v(41.28, -4.63) * mm, "end": v(41.2, -3.42) * mm});
            skLineSegment(sketch, "E805", {"start": v(41.2, -3.42) * mm, "end": v(41.08, -2.65) * mm});
            skLineSegment(sketch, "E806", {"start": v(41.08, -2.65) * mm, "end": v(41.02, -2.39) * mm});
            skLineSegment(sketch, "E807", {"start": v(41.02, -2.39) * mm, "end": v(41, -2.66) * mm});
            skLineSegment(sketch, "E808", {"start": v(41, -2.66) * mm, "end": v(40.9, -3.42) * mm});
            skLineSegment(sketch, "E809", {"start": v(40.9, -3.42) * mm, "end": v(40.7, -4.57) * mm});
            skLineSegment(sketch, "E810", {"start": v(40.7, -4.57) * mm, "end": v(40.35, -6.04) * mm});
            skLineSegment(sketch, "E811", {"start": v(40.35, -6.04) * mm, "end": v(40.24, -6.44) * mm});
            skLineSegment(sketch, "E812", {"start": v(40.24, -6.44) * mm, "end": v(40.1, -6.86) * mm});
            skLineSegment(sketch, "E813", {"start": v(40.1, -6.86) * mm, "end": v(39.8, -7.7) * mm});
            skLineSegment(sketch, "E814", {"start": v(39.8, -7.7) * mm, "end": v(39.42, -8.58) * mm});
            skLineSegment(sketch, "E815", {"start": v(39.42, -8.58) * mm, "end": v(38.97, -9.46) * mm});
            skLineSegment(sketch, "E816", {"start": v(38.97, -9.46) * mm, "end": v(38.44, -10.33) * mm});
            skLineSegment(sketch, "E817", {"start": v(38.44, -10.33) * mm, "end": v(38.2, -10.7) * mm});
            skLineSegment(sketch, "E818", {"start": v(38.2, -10.7) * mm, "end": v(36.8, -10.85) * mm});
            skLineSegment(sketch, "E819", {"start": v(36.8, -10.85) * mm, "end": v(35.92, -10.92) * mm});
            skLineSegment(sketch, "E820", {"start": v(35.92, -10.92) * mm, "end": v(35.04, -10.97) * mm});
            skLineSegment(sketch, "E821", {"start": v(35.04, -10.97) * mm, "end": v(34.16, -11) * mm});
            skLineSegment(sketch, "E822", {"start": v(34.16, -11) * mm, "end": v(33.73, -11.02) * mm});
            skLineSegment(sketch, "E823", {"start": v(33.73, -11.02) * mm, "end": v(33.3, -11.02) * mm});
            skLineSegment(sketch, "E824", {"start": v(33.3, -11.02) * mm, "end": v(31.57, -11) * mm});
            skLineSegment(sketch, "E825", {"start": v(31.57, -11) * mm, "end": v(30.72, -10.95) * mm});
            skLineSegment(sketch, "E826", {"start": v(30.72, -10.95) * mm, "end": v(29.89, -10.9) * mm});
            skLineSegment(sketch, "E827", {"start": v(29.89, -10.9) * mm, "end": v(26.72, -10.52) * mm});
            skLineSegment(sketch, "E828", {"start": v(26.72, -10.52) * mm, "end": v(23.9, -9.98) * mm});
            skLineSegment(sketch, "E829", {"start": v(23.9, -9.98) * mm, "end": v(23.26, -9.83) * mm});
            skLineSegment(sketch, "E830", {"start": v(23.26, -9.83) * mm, "end": v(22.65, -9.68) * mm});
            skLineSegment(sketch, "E831", {"start": v(22.65, -9.68) * mm, "end": v(21.53, -9.37) * mm});
            skLineSegment(sketch, "E832", {"start": v(21.53, -9.37) * mm, "end": v(19.73, -8.8) * mm});
            skLineSegment(sketch, "E833", {"start": v(19.73, -8.8) * mm, "end": v(18.59, -8.38) * mm});
            skLineSegment(sketch, "E834", {"start": v(18.59, -8.38) * mm, "end": v(18.19, -8.22) * mm});
            skLineSegment(sketch, "E835", {"start": v(18.19, -8.22) * mm, "end": v(18.28, -8.28) * mm});
            skLineSegment(sketch, "E836", {"start": v(18.28, -8.28) * mm, "end": v(18.55, -8.46) * mm});
            skLineSegment(sketch, "E837", {"start": v(18.55, -8.46) * mm, "end": v(19.6, -9.09) * mm});
            skLineSegment(sketch, "E838", {"start": v(19.6, -9.09) * mm, "end": v(21.33, -9.94) * mm});
            skLineSegment(sketch, "E839", {"start": v(21.33, -9.94) * mm, "end": v(23.65, -10.85) * mm});
            skLineSegment(sketch, "E840", {"start": v(23.65, -10.85) * mm, "end": v(25, -11.28) * mm});
            skLineSegment(sketch, "E841", {"start": v(25, -11.28) * mm, "end": v(26.49, -11.67) * mm});
            skLineSegment(sketch, "E842", {"start": v(26.49, -11.67) * mm, "end": v(29.74, -12.27) * mm});
            skLineSegment(sketch, "E843", {"start": v(29.74, -12.27) * mm, "end": v(31.48, -12.45) * mm});
            skLineSegment(sketch, "E844", {"start": v(31.48, -12.45) * mm, "end": v(32.38, -12.5) * mm});
            skLineSegment(sketch, "E845", {"start": v(32.38, -12.5) * mm, "end": v(32.83, -12.53) * mm});
            skLineSegment(sketch, "E846", {"start": v(32.83, -12.53) * mm, "end": v(33.28, -12.54) * mm});
            skLineSegment(sketch, "E847", {"start": v(33.28, -12.54) * mm, "end": v(36.74, -12.43) * mm});
            skLineSegment(sketch, "E848", {"start": v(36.74, -12.43) * mm, "end": v(36.43, -12.73) * mm});
            skLineSegment(sketch, "E849", {"start": v(36.43, -12.73) * mm, "end": v(34.78, -14.05) * mm});
            skLineSegment(sketch, "E850", {"start": v(34.78, -14.05) * mm, "end": v(34.34, -14.34) * mm});
            skLineSegment(sketch, "E851", {"start": v(34.34, -14.34) * mm, "end": v(33.9, -14.6) * mm});
            skLineSegment(sketch, "E852", {"start": v(33.9, -14.6) * mm, "end": v(33.68, -14.74) * mm});
            skLineSegment(sketch, "E853", {"start": v(33.68, -14.74) * mm, "end": v(33.45, -14.86) * mm});
            skLineSegment(sketch, "E854", {"start": v(33.45, -14.86) * mm, "end": v(33.23, -14.98) * mm});
            skLineSegment(sketch, "E855", {"start": v(33.23, -14.98) * mm, "end": v(33, -15.1) * mm});
            skLineSegment(sketch, "E856", {"start": v(33, -15.1) * mm, "end": v(31.22, -15.9) * mm});
            skLineSegment(sketch, "E857", {"start": v(31.22, -15.9) * mm, "end": v(30.36, -16.2) * mm});
            skLineSegment(sketch, "E858", {"start": v(30.36, -16.2) * mm, "end": v(29.94, -16.35) * mm});
            skLineSegment(sketch, "E859", {"start": v(29.94, -16.35) * mm, "end": v(29.54, -16.48) * mm});
            skLineSegment(sketch, "E860", {"start": v(29.54, -16.48) * mm, "end": v(28.78, -16.7) * mm});
            skLineSegment(sketch, "E861", {"start": v(28.78, -16.7) * mm, "end": v(28.08, -16.9) * mm});
            skLineSegment(sketch, "E862", {"start": v(28.08, -16.9) * mm, "end": v(27.46, -17.06) * mm});
            skLineSegment(sketch, "E863", {"start": v(27.46, -17.06) * mm, "end": v(26.93, -17.18) * mm});
            skLineSegment(sketch, "E864", {"start": v(26.93, -17.18) * mm, "end": v(26.19, -17.36) * mm});
            skLineSegment(sketch, "E865", {"start": v(26.19, -17.36) * mm, "end": v(25.92, -17.43) * mm});
            skLineSegment(sketch, "E866", {"start": v(25.92, -17.43) * mm, "end": v(26.2, -17.45) * mm});
            skLineSegment(sketch, "E867", {"start": v(26.2, -17.45) * mm, "end": v(26.52, -17.47) * mm});
            skLineSegment(sketch, "E868", {"start": v(26.52, -17.47) * mm, "end": v(26.73, -17.48) * mm});
            skLineSegment(sketch, "E869", {"start": v(26.73, -17.48) * mm, "end": v(26.96, -17.48) * mm});
            skLineSegment(sketch, "E870", {"start": v(26.96, -17.48) * mm, "end": v(27.52, -17.49) * mm});
            skLineSegment(sketch, "E871", {"start": v(27.52, -17.49) * mm, "end": v(28.17, -17.47) * mm});
            skLineSegment(sketch, "E872", {"start": v(28.17, -17.47) * mm, "end": v(28.9, -17.42) * mm});
            skLineSegment(sketch, "E873", {"start": v(28.9, -17.42) * mm, "end": v(29.3, -17.38) * mm});
            skLineSegment(sketch, "E874", {"start": v(29.3, -17.38) * mm, "end": v(29.73, -17.32) * mm});
            skLineSegment(sketch, "E875", {"start": v(29.73, -17.32) * mm, "end": v(31.56, -16.96) * mm});
            skLineSegment(sketch, "E876", {"start": v(31.56, -16.96) * mm, "end": v(33.55, -16.3) * mm});
            skLineSegment(sketch, "E877", {"start": v(33.55, -16.3) * mm, "end": v(34.06, -16.08) * mm});
            skLineSegment(sketch, "E878", {"start": v(34.06, -16.08) * mm, "end": v(34.32, -15.96) * mm});
            skLineSegment(sketch, "E879", {"start": v(34.32, -15.96) * mm, "end": v(34.57, -15.83) * mm});
            skLineSegment(sketch, "E880", {"start": v(34.57, -15.83) * mm, "end": v(35.57, -15.26) * mm});
            skLineSegment(sketch, "E881", {"start": v(35.57, -15.26) * mm, "end": v(35.82, -15.1) * mm});
            skLineSegment(sketch, "E882", {"start": v(35.82, -15.1) * mm, "end": v(36.06, -14.94) * mm});
            skLineSegment(sketch, "E883", {"start": v(36.06, -14.94) * mm, "end": v(36.54, -14.59) * mm});
            skLineSegment(sketch, "E884", {"start": v(36.54, -14.59) * mm, "end": v(37.45, -13.82) * mm});
            skLineSegment(sketch, "E885", {"start": v(37.45, -13.82) * mm, "end": v(38.27, -12.96) * mm});
            skLineSegment(sketch, "E886", {"start": v(38.27, -12.96) * mm, "end": v(38.65, -12.5) * mm});
            skLineSegment(sketch, "E887", {"start": v(38.65, -12.5) * mm, "end": v(38.83, -12.27) * mm});
            skLineSegment(sketch, "E888", {"start": v(38.83, -12.27) * mm, "end": v(38.9, -12.17) * mm});
            skLineSegment(sketch, "E889", {"start": v(38.9, -12.17) * mm, "end": v(40.57, -11.87) * mm});
            skLineSegment(sketch, "E890", {"start": v(40.57, -11.87) * mm, "end": v(42.31, -11.47) * mm});
            skLineSegment(sketch, "E891", {"start": v(42.31, -11.47) * mm, "end": v(44, -10.98) * mm});
            skLineSegment(sketch, "E892", {"start": v(44, -10.98) * mm, "end": v(47.1, -9.83) * mm});
            skLineSegment(sketch, "E893", {"start": v(47.1, -9.83) * mm, "end": v(49.75, -8.55) * mm});
            skLineSegment(sketch, "E894", {"start": v(49.75, -8.55) * mm, "end": v(50.34, -8.23) * mm});
            skLineSegment(sketch, "E895", {"start": v(50.34, -8.23) * mm, "end": v(50.9, -7.91) * mm});
            skLineSegment(sketch, "E896", {"start": v(50.9, -7.91) * mm, "end": v(51.9, -7.3) * mm});
            skLineSegment(sketch, "E897", {"start": v(51.9, -7.3) * mm, "end": v(52.77, -6.73) * mm});
            skLineSegment(sketch, "E898", {"start": v(52.77, -6.73) * mm, "end": v(53.5, -6.23) * mm});
            skLineSegment(sketch, "E899", {"start": v(53.5, -6.23) * mm, "end": v(54.48, -5.5) * mm});
            skLineSegment(sketch, "E900", {"start": v(54.48, -5.5) * mm, "end": v(54.82, -5.23) * mm});
            skLineSegment(sketch, "E901", {"start": v(54.82, -5.23) * mm, "end": v(54.43, -5.42) * mm});
            skLineSegment(sketch, "E902", {"start": v(44.96, -7.93) * mm, "end": v(44.5, -8.43) * mm});
            skLineSegment(sketch, "E903", {"start": v(44.5, -8.43) * mm, "end": v(43.98, -8.72) * mm});
            skLineSegment(sketch, "E904", {"start": v(43.98, -8.72) * mm, "end": v(43.44, -8.8) * mm});
            skLineSegment(sketch, "E905", {"start": v(43.44, -8.8) * mm, "end": v(42.95, -8.63) * mm});
            skLineSegment(sketch, "E906", {"start": v(42.95, -8.63) * mm, "end": v(42.61, -8.25) * mm});
            skLineSegment(sketch, "E907", {"start": v(42.61, -8.25) * mm, "end": v(42.48, -7.72) * mm});
            skLineSegment(sketch, "E908", {"start": v(42.48, -7.72) * mm, "end": v(42.56, -7.12) * mm});
            skLineSegment(sketch, "E909", {"start": v(42.56, -7.12) * mm, "end": v(42.85, -6.51) * mm});
            skLineSegment(sketch, "E910", {"start": v(42.85, -6.51) * mm, "end": v(43.3, -6.02) * mm});
            skLineSegment(sketch, "E911", {"start": v(43.3, -6.02) * mm, "end": v(43.83, -5.72) * mm});
            skLineSegment(sketch, "E912", {"start": v(43.83, -5.72) * mm, "end": v(44.37, -5.64) * mm});
            skLineSegment(sketch, "E913", {"start": v(44.37, -5.64) * mm, "end": v(44.85, -5.8) * mm});
            skLineSegment(sketch, "E914", {"start": v(44.85, -5.8) * mm, "end": v(45.19, -6.2) * mm});
            skLineSegment(sketch, "E915", {"start": v(45.19, -6.2) * mm, "end": v(45.32, -6.73) * mm});
            skLineSegment(sketch, "E916", {"start": v(45.32, -6.73) * mm, "end": v(45.25, -7.33) * mm});
            skLineSegment(sketch, "E917", {"start": v(45.25, -7.33) * mm, "end": v(44.96, -7.93) * mm});
            skLineSegment(sketch, "E918", {"start": v(54.63, -5.74) * mm, "end": v(54.16, -5.97) * mm});
            skLineSegment(sketch, "E919", {"start": v(54.16, -5.97) * mm, "end": v(53.87, -6.12) * mm});
            skLineSegment(sketch, "E920", {"start": v(53.87, -6.12) * mm, "end": v(53.53, -6.28) * mm});
            skLineSegment(sketch, "E921", {"start": v(53.53, -6.28) * mm, "end": v(52.75, -6.66) * mm});
            skLineSegment(sketch, "E922", {"start": v(52.75, -6.66) * mm, "end": v(51.82, -7.08) * mm});
            skLineSegment(sketch, "E923", {"start": v(51.82, -7.08) * mm, "end": v(51.3, -7.31) * mm});
            skLineSegment(sketch, "E924", {"start": v(51.3, -7.31) * mm, "end": v(50.75, -7.55) * mm});
            skLineSegment(sketch, "E925", {"start": v(50.75, -7.55) * mm, "end": v(50.18, -7.8) * mm});
            skLineSegment(sketch, "E926", {"start": v(50.18, -7.8) * mm, "end": v(49.57, -8.04) * mm});
            skLineSegment(sketch, "E927", {"start": v(49.57, -8.04) * mm, "end": v(48.93, -8.3) * mm});
            skLineSegment(sketch, "E928", {"start": v(48.93, -8.3) * mm, "end": v(48.27, -8.55) * mm});
            skLineSegment(sketch, "E929", {"start": v(48.27, -8.55) * mm, "end": v(47.58, -8.8) * mm});
            skLineSegment(sketch, "E930", {"start": v(47.58, -8.8) * mm, "end": v(46.87, -9.04) * mm});
            skLineSegment(sketch, "E931", {"start": v(46.87, -9.04) * mm, "end": v(43.8, -9.96) * mm});
            skLineSegment(sketch, "E932", {"start": v(43.8, -9.96) * mm, "end": v(43, -10.17) * mm});
            skLineSegment(sketch, "E933", {"start": v(43, -10.17) * mm, "end": v(42.17, -10.36) * mm});
            skLineSegment(sketch, "E934", {"start": v(42.17, -10.36) * mm, "end": v(41.33, -10.53) * mm});
            skLineSegment(sketch, "E935", {"start": v(41.33, -10.53) * mm, "end": v(40.48, -10.7) * mm});
            skLineSegment(sketch, "E936", {"start": v(40.48, -10.7) * mm, "end": v(40.16, -10.75) * mm});
            skLineSegment(sketch, "E937", {"start": v(40.16, -10.75) * mm, "end": v(40.35, -10.37) * mm});
            skLineSegment(sketch, "E938", {"start": v(40.35, -10.37) * mm, "end": v(40.75, -9.36) * mm});
            skLineSegment(sketch, "E939", {"start": v(40.75, -9.36) * mm, "end": v(41.05, -8.37) * mm});
            skLineSegment(sketch, "E940", {"start": v(41.05, -8.37) * mm, "end": v(41.4, -6.52) * mm});
            skLineSegment(sketch, "E941", {"start": v(41.4, -6.52) * mm, "end": v(41.48, -4.94) * mm});
            skLineSegment(sketch, "E942", {"start": v(41.48, -4.94) * mm, "end": v(41.4, -3.74) * mm});
            skLineSegment(sketch, "E943", {"start": v(41.4, -3.74) * mm, "end": v(41.28, -2.97) * mm});
            skLineSegment(sketch, "E944", {"start": v(41.28, -2.97) * mm, "end": v(41.22, -2.7) * mm});
            skLineSegment(sketch, "E945", {"start": v(41.22, -2.7) * mm, "end": v(41.2, -2.97) * mm});
            skLineSegment(sketch, "E946", {"start": v(41.2, -2.97) * mm, "end": v(41.1, -3.73) * mm});
            skLineSegment(sketch, "E947", {"start": v(41.1, -3.73) * mm, "end": v(40.9, -4.9) * mm});
            skLineSegment(sketch, "E948", {"start": v(40.9, -4.9) * mm, "end": v(40.55, -6.36) * mm});
            skLineSegment(sketch, "E949", {"start": v(40.55, -6.36) * mm, "end": v(40.44, -6.76) * mm});
            skLineSegment(sketch, "E950", {"start": v(40.44, -6.76) * mm, "end": v(40.3, -7.17) * mm});
            skLineSegment(sketch, "E951", {"start": v(40.3, -7.17) * mm, "end": v(40, -8.02) * mm});
            skLineSegment(sketch, "E952", {"start": v(40, -8.02) * mm, "end": v(39.61, -8.9) * mm});
            skLineSegment(sketch, "E953", {"start": v(39.61, -8.9) * mm, "end": v(39.16, -9.78) * mm});
            skLineSegment(sketch, "E954", {"start": v(39.16, -9.78) * mm, "end": v(38.64, -10.65) * mm});
            skLineSegment(sketch, "E955", {"start": v(38.64, -10.65) * mm, "end": v(38.4, -11.02) * mm});
            skLineSegment(sketch, "E956", {"start": v(38.4, -11.02) * mm, "end": v(37, -11.17) * mm});
            skLineSegment(sketch, "E957", {"start": v(37, -11.17) * mm, "end": v(36.12, -11.24) * mm});
            skLineSegment(sketch, "E958", {"start": v(36.12, -11.24) * mm, "end": v(35.24, -11.29) * mm});
            skLineSegment(sketch, "E959", {"start": v(35.24, -11.29) * mm, "end": v(34.36, -11.32) * mm});
            skLineSegment(sketch, "E960", {"start": v(34.36, -11.32) * mm, "end": v(33.93, -11.33) * mm});
            skLineSegment(sketch, "E961", {"start": v(33.93, -11.33) * mm, "end": v(33.49, -11.34) * mm});
            skLineSegment(sketch, "E962", {"start": v(33.49, -11.34) * mm, "end": v(31.77, -11.3) * mm});
            skLineSegment(sketch, "E963", {"start": v(31.77, -11.3) * mm, "end": v(30.92, -11.27) * mm});
            skLineSegment(sketch, "E964", {"start": v(30.92, -11.27) * mm, "end": v(30.09, -11.21) * mm});
            skLineSegment(sketch, "E965", {"start": v(30.09, -11.21) * mm, "end": v(26.91, -10.84) * mm});
            skLineSegment(sketch, "E966", {"start": v(26.91, -10.84) * mm, "end": v(24.1, -10.3) * mm});
            skLineSegment(sketch, "E967", {"start": v(24.1, -10.3) * mm, "end": v(23.46, -10.15) * mm});
            skLineSegment(sketch, "E968", {"start": v(23.46, -10.15) * mm, "end": v(22.85, -10) * mm});
            skLineSegment(sketch, "E969", {"start": v(22.85, -10) * mm, "end": v(21.73, -9.69) * mm});
            skLineSegment(sketch, "E970", {"start": v(21.73, -9.69) * mm, "end": v(19.93, -9.12) * mm});
            skLineSegment(sketch, "E971", {"start": v(19.93, -9.12) * mm, "end": v(18.78, -8.7) * mm});
            skLineSegment(sketch, "E972", {"start": v(18.78, -8.7) * mm, "end": v(18.38, -8.53) * mm});
            skLineSegment(sketch, "E973", {"start": v(18.38, -8.53) * mm, "end": v(18.47, -8.6) * mm});
            skLineSegment(sketch, "E974", {"start": v(18.47, -8.6) * mm, "end": v(18.74, -8.78) * mm});
            skLineSegment(sketch, "E975", {"start": v(18.74, -8.78) * mm, "end": v(19.8, -9.4) * mm});
            skLineSegment(sketch, "E976", {"start": v(19.8, -9.4) * mm, "end": v(21.52, -10.25) * mm});
            skLineSegment(sketch, "E977", {"start": v(21.52, -10.25) * mm, "end": v(23.84, -11.17) * mm});
            skLineSegment(sketch, "E978", {"start": v(23.84, -11.17) * mm, "end": v(25.2, -11.6) * mm});
            skLineSegment(sketch, "E979", {"start": v(25.2, -11.6) * mm, "end": v(26.69, -11.99) * mm});
            skLineSegment(sketch, "E980", {"start": v(26.69, -11.99) * mm, "end": v(29.94, -12.59) * mm});
            skLineSegment(sketch, "E981", {"start": v(29.94, -12.59) * mm, "end": v(31.68, -12.77) * mm});
            skLineSegment(sketch, "E982", {"start": v(31.68, -12.77) * mm, "end": v(32.57, -12.82) * mm});
            skLineSegment(sketch, "E983", {"start": v(32.57, -12.82) * mm, "end": v(33.03, -12.84) * mm});
            skLineSegment(sketch, "E984", {"start": v(33.03, -12.84) * mm, "end": v(33.48, -12.85) * mm});
            skLineSegment(sketch, "E985", {"start": v(33.48, -12.85) * mm, "end": v(36.94, -12.74) * mm});
            skLineSegment(sketch, "E986", {"start": v(36.94, -12.74) * mm, "end": v(36.63, -13.05) * mm});
            skLineSegment(sketch, "E987", {"start": v(36.63, -13.05) * mm, "end": v(34.98, -14.36) * mm});
            skLineSegment(sketch, "E988", {"start": v(34.98, -14.36) * mm, "end": v(34.54, -14.65) * mm});
            skLineSegment(sketch, "E989", {"start": v(34.54, -14.65) * mm, "end": v(34.1, -14.92) * mm});
            skLineSegment(sketch, "E990", {"start": v(34.1, -14.92) * mm, "end": v(33.88, -15.05) * mm});
            skLineSegment(sketch, "E991", {"start": v(33.88, -15.05) * mm, "end": v(33.65, -15.17) * mm});
            skLineSegment(sketch, "E992", {"start": v(33.65, -15.17) * mm, "end": v(33.43, -15.3) * mm});
            skLineSegment(sketch, "E993", {"start": v(33.43, -15.3) * mm, "end": v(33.2, -15.41) * mm});
            skLineSegment(sketch, "E994", {"start": v(33.2, -15.41) * mm, "end": v(31.41, -16.21) * mm});
            skLineSegment(sketch, "E995", {"start": v(31.41, -16.21) * mm, "end": v(30.55, -16.52) * mm});
            skLineSegment(sketch, "E996", {"start": v(30.55, -16.52) * mm, "end": v(30.14, -16.67) * mm});
            skLineSegment(sketch, "E997", {"start": v(30.14, -16.67) * mm, "end": v(29.74, -16.8) * mm});
            skLineSegment(sketch, "E998", {"start": v(29.74, -16.8) * mm, "end": v(28.97, -17.03) * mm});
            skLineSegment(sketch, "E999", {"start": v(28.97, -17.03) * mm, "end": v(28.28, -17.22) * mm});
            skLineSegment(sketch, "E1000", {"start": v(28.28, -17.22) * mm, "end": v(27.66, -17.37) * mm});
            skLineSegment(sketch, "E1001", {"start": v(27.66, -17.37) * mm, "end": v(27.13, -17.5) * mm});
            skLineSegment(sketch, "E1002", {"start": v(27.13, -17.5) * mm, "end": v(26.38, -17.68) * mm});
            skLineSegment(sketch, "E1003", {"start": v(26.38, -17.68) * mm, "end": v(26.12, -17.74) * mm});
            skLineSegment(sketch, "E1004", {"start": v(26.12, -17.74) * mm, "end": v(26.4, -17.77) * mm});
            skLineSegment(sketch, "E1005", {"start": v(26.4, -17.77) * mm, "end": v(26.72, -17.79) * mm});
            skLineSegment(sketch, "E1006", {"start": v(26.72, -17.79) * mm, "end": v(26.93, -17.8) * mm});
            skLineSegment(sketch, "E1007", {"start": v(26.93, -17.8) * mm, "end": v(27.16, -17.8) * mm});
            skLineSegment(sketch, "E1008", {"start": v(27.16, -17.8) * mm, "end": v(27.71, -17.8) * mm});
            skLineSegment(sketch, "E1009", {"start": v(27.71, -17.8) * mm, "end": v(28.36, -17.78) * mm});
            skLineSegment(sketch, "E1010", {"start": v(28.36, -17.78) * mm, "end": v(29.1, -17.74) * mm});
            skLineSegment(sketch, "E1011", {"start": v(29.1, -17.74) * mm, "end": v(29.5, -17.7) * mm});
            skLineSegment(sketch, "E1012", {"start": v(29.5, -17.7) * mm, "end": v(29.93, -17.64) * mm});
            skLineSegment(sketch, "E1013", {"start": v(29.93, -17.64) * mm, "end": v(31.76, -17.28) * mm});
            skLineSegment(sketch, "E1014", {"start": v(31.76, -17.28) * mm, "end": v(33.75, -16.62) * mm});
            skLineSegment(sketch, "E1015", {"start": v(33.75, -16.62) * mm, "end": v(34.26, -16.4) * mm});
            skLineSegment(sketch, "E1016", {"start": v(34.26, -16.4) * mm, "end": v(34.52, -16.27) * mm});
            skLineSegment(sketch, "E1017", {"start": v(34.52, -16.27) * mm, "end": v(34.77, -16.14) * mm});
            skLineSegment(sketch, "E1018", {"start": v(34.77, -16.14) * mm, "end": v(35.77, -15.58) * mm});
            skLineSegment(sketch, "E1019", {"start": v(35.77, -15.58) * mm, "end": v(36.02, -15.42) * mm});
            skLineSegment(sketch, "E1020", {"start": v(36.02, -15.42) * mm, "end": v(36.26, -15.25) * mm});
            skLineSegment(sketch, "E1021", {"start": v(36.26, -15.25) * mm, "end": v(36.74, -14.9) * mm});
            skLineSegment(sketch, "E1022", {"start": v(36.74, -14.9) * mm, "end": v(37.64, -14.13) * mm});
            skLineSegment(sketch, "E1023", {"start": v(37.64, -14.13) * mm, "end": v(38.47, -13.28) * mm});
            skLineSegment(sketch, "E1024", {"start": v(38.47, -13.28) * mm, "end": v(38.85, -12.82) * mm});
            skLineSegment(sketch, "E1025", {"start": v(38.85, -12.82) * mm, "end": v(39.03, -12.59) * mm});
            skLineSegment(sketch, "E1026", {"start": v(39.03, -12.59) * mm, "end": v(39.1, -12.48) * mm});
            skLineSegment(sketch, "E1027", {"start": v(39.1, -12.48) * mm, "end": v(40.76, -12.19) * mm});
            skLineSegment(sketch, "E1028", {"start": v(40.76, -12.19) * mm, "end": v(42.51, -11.78) * mm});
            skLineSegment(sketch, "E1029", {"start": v(42.51, -11.78) * mm, "end": v(44.2, -11.3) * mm});
            skLineSegment(sketch, "E1030", {"start": v(44.2, -11.3) * mm, "end": v(47.3, -10.14) * mm});
            skLineSegment(sketch, "E1031", {"start": v(47.3, -10.14) * mm, "end": v(49.95, -8.87) * mm});
            skLineSegment(sketch, "E1032", {"start": v(49.95, -8.87) * mm, "end": v(50.54, -8.54) * mm});
            skLineSegment(sketch, "E1033", {"start": v(50.54, -8.54) * mm, "end": v(51.1, -8.23) * mm});
            skLineSegment(sketch, "E1034", {"start": v(51.1, -8.23) * mm, "end": v(52.1, -7.61) * mm});
            skLineSegment(sketch, "E1035", {"start": v(52.1, -7.61) * mm, "end": v(52.97, -7.05) * mm});
            skLineSegment(sketch, "E1036", {"start": v(52.97, -7.05) * mm, "end": v(53.7, -6.55) * mm});
            skLineSegment(sketch, "E1037", {"start": v(53.7, -6.55) * mm, "end": v(54.68, -5.81) * mm});
            skLineSegment(sketch, "E1038", {"start": v(54.68, -5.81) * mm, "end": v(55.02, -5.55) * mm});
            skLineSegment(sketch, "E1039", {"start": v(55.02, -5.55) * mm, "end": v(54.63, -5.74) * mm});
            skLineSegment(sketch, "E1040", {"start": v(45.31, -8.34) * mm, "end": v(44.86, -8.84) * mm});
            skLineSegment(sketch, "E1041", {"start": v(44.86, -8.84) * mm, "end": v(44.33, -9.13) * mm});
            skLineSegment(sketch, "E1042", {"start": v(44.33, -9.13) * mm, "end": v(43.79, -9.2) * mm});
            skLineSegment(sketch, "E1043", {"start": v(43.79, -9.2) * mm, "end": v(43.3, -9.04) * mm});
            skLineSegment(sketch, "E1044", {"start": v(43.3, -9.04) * mm, "end": v(42.97, -8.65) * mm});
            skLineSegment(sketch, "E1045", {"start": v(42.97, -8.65) * mm, "end": v(42.83, -8.13) * mm});
            skLineSegment(sketch, "E1046", {"start": v(42.83, -8.13) * mm, "end": v(42.9, -7.52) * mm});
            skLineSegment(sketch, "E1047", {"start": v(42.9, -7.52) * mm, "end": v(43.2, -6.92) * mm});
            skLineSegment(sketch, "E1048", {"start": v(43.2, -6.92) * mm, "end": v(43.65, -6.43) * mm});
            skLineSegment(sketch, "E1049", {"start": v(43.65, -6.43) * mm, "end": v(44.18, -6.13) * mm});
            skLineSegment(sketch, "E1050", {"start": v(44.18, -6.13) * mm, "end": v(44.72, -6.05) * mm});
            skLineSegment(sketch, "E1051", {"start": v(44.72, -6.05) * mm, "end": v(45.2, -6.22) * mm});
            skLineSegment(sketch, "E1052", {"start": v(45.2, -6.22) * mm, "end": v(45.54, -6.6) * mm});
            skLineSegment(sketch, "E1053", {"start": v(45.54, -6.6) * mm, "end": v(45.67, -7.14) * mm});
            skLineSegment(sketch, "E1054", {"start": v(45.67, -7.14) * mm, "end": v(45.6, -7.74) * mm});
            skLineSegment(sketch, "E1055", {"start": v(45.6, -7.74) * mm, "end": v(45.31, -8.34) * mm});
            skLineSegment(sketch, "E1056", {"start": v(54.98, -6.15) * mm, "end": v(54.52, -6.38) * mm});
            skLineSegment(sketch, "E1057", {"start": v(54.52, -6.38) * mm, "end": v(54.22, -6.52) * mm});
            skLineSegment(sketch, "E1058", {"start": v(54.22, -6.52) * mm, "end": v(53.88, -6.69) * mm});
            skLineSegment(sketch, "E1059", {"start": v(53.88, -6.69) * mm, "end": v(53.1, -7.06) * mm});
            skLineSegment(sketch, "E1060", {"start": v(53.1, -7.06) * mm, "end": v(52.17, -7.5) * mm});
            skLineSegment(sketch, "E1061", {"start": v(52.17, -7.5) * mm, "end": v(51.65, -7.72) * mm});
            skLineSegment(sketch, "E1062", {"start": v(51.65, -7.72) * mm, "end": v(51.1, -7.96) * mm});
            skLineSegment(sketch, "E1063", {"start": v(51.1, -7.96) * mm, "end": v(50.53, -8.2) * mm});
            skLineSegment(sketch, "E1064", {"start": v(50.53, -8.2) * mm, "end": v(49.92, -8.45) * mm});
            skLineSegment(sketch, "E1065", {"start": v(49.92, -8.45) * mm, "end": v(49.28, -8.7) * mm});
            skLineSegment(sketch, "E1066", {"start": v(49.28, -8.7) * mm, "end": v(48.62, -8.96) * mm});
            skLineSegment(sketch, "E1067", {"start": v(48.62, -8.96) * mm, "end": v(47.93, -9.2) * mm});
            skLineSegment(sketch, "E1068", {"start": v(47.93, -9.2) * mm, "end": v(47.22, -9.45) * mm});
            skLineSegment(sketch, "E1069", {"start": v(47.22, -9.45) * mm, "end": v(44.16, -10.37) * mm});
            skLineSegment(sketch, "E1070", {"start": v(44.16, -10.37) * mm, "end": v(43.35, -10.58) * mm});
            skLineSegment(sketch, "E1071", {"start": v(43.35, -10.58) * mm, "end": v(42.52, -10.77) * mm});
            skLineSegment(sketch, "E1072", {"start": v(42.52, -10.77) * mm, "end": v(41.68, -10.94) * mm});
            skLineSegment(sketch, "E1073", {"start": v(41.68, -10.94) * mm, "end": v(40.83, -11.1) * mm});
            skLineSegment(sketch, "E1074", {"start": v(40.83, -11.1) * mm, "end": v(40.51, -11.16) * mm});
            skLineSegment(sketch, "E1075", {"start": v(40.51, -11.16) * mm, "end": v(40.7, -10.78) * mm});
            skLineSegment(sketch, "E1076", {"start": v(40.7, -10.78) * mm, "end": v(41.1, -9.77) * mm});
            skLineSegment(sketch, "E1077", {"start": v(41.1, -9.77) * mm, "end": v(41.4, -8.78) * mm});
            skLineSegment(sketch, "E1078", {"start": v(41.4, -8.78) * mm, "end": v(41.75, -6.93) * mm});
            skLineSegment(sketch, "E1079", {"start": v(41.75, -6.93) * mm, "end": v(41.83, -5.35) * mm});
            skLineSegment(sketch, "E1080", {"start": v(41.83, -5.35) * mm, "end": v(41.75, -4.14) * mm});
            skLineSegment(sketch, "E1081", {"start": v(41.75, -4.14) * mm, "end": v(41.63, -3.38) * mm});
            skLineSegment(sketch, "E1082", {"start": v(41.63, -3.38) * mm, "end": v(41.57, -3.11) * mm});
            skLineSegment(sketch, "E1083", {"start": v(41.57, -3.11) * mm, "end": v(41.55, -3.38) * mm});
            skLineSegment(sketch, "E1084", {"start": v(41.55, -3.38) * mm, "end": v(41.45, -4.14) * mm});
            skLineSegment(sketch, "E1085", {"start": v(41.45, -4.14) * mm, "end": v(41.26, -5.3) * mm});
            skLineSegment(sketch, "E1086", {"start": v(41.26, -5.3) * mm, "end": v(40.9, -6.77) * mm});
            skLineSegment(sketch, "E1087", {"start": v(40.9, -6.77) * mm, "end": v(40.79, -7.17) * mm});
            skLineSegment(sketch, "E1088", {"start": v(40.79, -7.17) * mm, "end": v(40.65, -7.58) * mm});
            skLineSegment(sketch, "E1089", {"start": v(40.65, -7.58) * mm, "end": v(40.34, -8.43) * mm});
            skLineSegment(sketch, "E1090", {"start": v(40.34, -8.43) * mm, "end": v(39.96, -9.3) * mm});
            skLineSegment(sketch, "E1091", {"start": v(39.96, -9.3) * mm, "end": v(39.52, -10.19) * mm});
            skLineSegment(sketch, "E1092", {"start": v(39.52, -10.19) * mm, "end": v(39, -11.06) * mm});
            skLineSegment(sketch, "E1093", {"start": v(39, -11.06) * mm, "end": v(38.74, -11.42) * mm});
            skLineSegment(sketch, "E1094", {"start": v(38.74, -11.42) * mm, "end": v(37.35, -11.58) * mm});
            skLineSegment(sketch, "E1095", {"start": v(37.35, -11.58) * mm, "end": v(36.47, -11.65) * mm});
            skLineSegment(sketch, "E1096", {"start": v(36.47, -11.65) * mm, "end": v(35.6, -11.7) * mm});
            skLineSegment(sketch, "E1097", {"start": v(35.6, -11.7) * mm, "end": v(34.71, -11.73) * mm});
            skLineSegment(sketch, "E1098", {"start": v(34.71, -11.73) * mm, "end": v(34.28, -11.74) * mm});
            skLineSegment(sketch, "E1099", {"start": v(34.28, -11.74) * mm, "end": v(33.84, -11.75) * mm});
            skLineSegment(sketch, "E1100", {"start": v(33.84, -11.75) * mm, "end": v(32.12, -11.72) * mm});
            skLineSegment(sketch, "E1101", {"start": v(32.12, -11.72) * mm, "end": v(31.27, -11.68) * mm});
            skLineSegment(sketch, "E1102", {"start": v(31.27, -11.68) * mm, "end": v(30.44, -11.62) * mm});
            skLineSegment(sketch, "E1103", {"start": v(30.44, -11.62) * mm, "end": v(27.26, -11.25) * mm});
            skLineSegment(sketch, "E1104", {"start": v(27.26, -11.25) * mm, "end": v(24.44, -10.7) * mm});
            skLineSegment(sketch, "E1105", {"start": v(24.44, -10.7) * mm, "end": v(23.8, -10.56) * mm});
            skLineSegment(sketch, "E1106", {"start": v(23.8, -10.56) * mm, "end": v(23.2, -10.4) * mm});
            skLineSegment(sketch, "E1107", {"start": v(23.2, -10.4) * mm, "end": v(22.08, -10.1) * mm});
            skLineSegment(sketch, "E1108", {"start": v(22.08, -10.1) * mm, "end": v(20.28, -9.53) * mm});
            skLineSegment(sketch, "E1109", {"start": v(20.28, -9.53) * mm, "end": v(19.14, -9.1) * mm});
            skLineSegment(sketch, "E1110", {"start": v(19.14, -9.1) * mm, "end": v(18.73, -8.94) * mm});
            skLineSegment(sketch, "E1111", {"start": v(18.73, -8.94) * mm, "end": v(18.83, -9) * mm});
            skLineSegment(sketch, "E1112", {"start": v(18.83, -9) * mm, "end": v(19.1, -9.19) * mm});
            skLineSegment(sketch, "E1113", {"start": v(19.1, -9.19) * mm, "end": v(20.16, -9.81) * mm});
            skLineSegment(sketch, "E1114", {"start": v(20.16, -9.81) * mm, "end": v(21.87, -10.66) * mm});
            skLineSegment(sketch, "E1115", {"start": v(21.87, -10.66) * mm, "end": v(24.2, -11.57) * mm});
            skLineSegment(sketch, "E1116", {"start": v(24.2, -11.57) * mm, "end": v(25.56, -12) * mm});
            skLineSegment(sketch, "E1117", {"start": v(25.56, -12) * mm, "end": v(27.04, -12.4) * mm});
            skLineSegment(sketch, "E1118", {"start": v(27.04, -12.4) * mm, "end": v(30.3, -13) * mm});
            skLineSegment(sketch, "E1119", {"start": v(30.3, -13) * mm, "end": v(32.03, -13.18) * mm});
            skLineSegment(sketch, "E1120", {"start": v(32.03, -13.18) * mm, "end": v(32.93, -13.24) * mm});
            skLineSegment(sketch, "E1121", {"start": v(32.93, -13.24) * mm, "end": v(33.38, -13.25) * mm});
            skLineSegment(sketch, "E1122", {"start": v(33.38, -13.25) * mm, "end": v(33.83, -13.26) * mm});
            skLineSegment(sketch, "E1123", {"start": v(33.83, -13.26) * mm, "end": v(37.3, -13.15) * mm});
            skLineSegment(sketch, "E1124", {"start": v(37.3, -13.15) * mm, "end": v(36.98, -13.46) * mm});
            skLineSegment(sketch, "E1125", {"start": v(36.98, -13.46) * mm, "end": v(35.33, -14.77) * mm});
            skLineSegment(sketch, "E1126", {"start": v(35.33, -14.77) * mm, "end": v(34.9, -15.06) * mm});
            skLineSegment(sketch, "E1127", {"start": v(34.9, -15.06) * mm, "end": v(34.45, -15.33) * mm});
            skLineSegment(sketch, "E1128", {"start": v(34.45, -15.33) * mm, "end": v(34.23, -15.46) * mm});
            skLineSegment(sketch, "E1129", {"start": v(34.23, -15.46) * mm, "end": v(34, -15.59) * mm});
            skLineSegment(sketch, "E1130", {"start": v(34, -15.59) * mm, "end": v(33.78, -15.7) * mm});
            skLineSegment(sketch, "E1131", {"start": v(33.78, -15.7) * mm, "end": v(33.55, -15.82) * mm});
            skLineSegment(sketch, "E1132", {"start": v(33.55, -15.82) * mm, "end": v(31.76, -16.62) * mm});
            skLineSegment(sketch, "E1133", {"start": v(31.76, -16.62) * mm, "end": v(30.9, -16.93) * mm});
            skLineSegment(sketch, "E1134", {"start": v(30.9, -16.93) * mm, "end": v(30.5, -17.08) * mm});
            skLineSegment(sketch, "E1135", {"start": v(30.5, -17.08) * mm, "end": v(30.09, -17.2) * mm});
            skLineSegment(sketch, "E1136", {"start": v(30.09, -17.2) * mm, "end": v(29.33, -17.43) * mm});
            skLineSegment(sketch, "E1137", {"start": v(29.33, -17.43) * mm, "end": v(28.63, -17.63) * mm});
            skLineSegment(sketch, "E1138", {"start": v(28.63, -17.63) * mm, "end": v(28.01, -17.78) * mm});
            skLineSegment(sketch, "E1139", {"start": v(28.01, -17.78) * mm, "end": v(27.48, -17.91) * mm});
            skLineSegment(sketch, "E1140", {"start": v(27.48, -17.91) * mm, "end": v(26.74, -18.09) * mm});
            skLineSegment(sketch, "E1141", {"start": v(26.74, -18.09) * mm, "end": v(26.47, -18.15) * mm});
            skLineSegment(sketch, "E1142", {"start": v(26.47, -18.15) * mm, "end": v(26.74, -18.17) * mm});
            skLineSegment(sketch, "E1143", {"start": v(26.74, -18.17) * mm, "end": v(27.07, -18.2) * mm});
            skLineSegment(sketch, "E1144", {"start": v(27.07, -18.2) * mm, "end": v(27.28, -18.2) * mm});
            skLineSegment(sketch, "E1145", {"start": v(27.28, -18.2) * mm, "end": v(27.51, -18.2) * mm});
            skLineSegment(sketch, "E1146", {"start": v(27.51, -18.2) * mm, "end": v(28.06, -18.21) * mm});
            skLineSegment(sketch, "E1147", {"start": v(28.06, -18.21) * mm, "end": v(28.72, -18.2) * mm});
            skLineSegment(sketch, "E1148", {"start": v(28.72, -18.2) * mm, "end": v(29.46, -18.15) * mm});
            skLineSegment(sketch, "E1149", {"start": v(29.46, -18.15) * mm, "end": v(29.86, -18.1) * mm});
            skLineSegment(sketch, "E1150", {"start": v(29.86, -18.1) * mm, "end": v(30.28, -18.05) * mm});
            skLineSegment(sketch, "E1151", {"start": v(30.28, -18.05) * mm, "end": v(32.1, -17.69) * mm});
            skLineSegment(sketch, "E1152", {"start": v(32.1, -17.69) * mm, "end": v(34.1, -17.03) * mm});
            skLineSegment(sketch, "E1153", {"start": v(34.1, -17.03) * mm, "end": v(34.61, -16.8) * mm});
            skLineSegment(sketch, "E1154", {"start": v(34.61, -16.8) * mm, "end": v(34.87, -16.68) * mm});
            skLineSegment(sketch, "E1155", {"start": v(34.87, -16.68) * mm, "end": v(35.12, -16.56) * mm});
            skLineSegment(sketch, "E1156", {"start": v(35.12, -16.56) * mm, "end": v(36.12, -15.98) * mm});
            skLineSegment(sketch, "E1157", {"start": v(36.12, -15.98) * mm, "end": v(36.37, -15.83) * mm});
            skLineSegment(sketch, "E1158", {"start": v(36.37, -15.83) * mm, "end": v(36.61, -15.66) * mm});
            skLineSegment(sketch, "E1159", {"start": v(36.61, -15.66) * mm, "end": v(37.09, -15.31) * mm});
            skLineSegment(sketch, "E1160", {"start": v(37.09, -15.31) * mm, "end": v(38, -14.54) * mm});
            skLineSegment(sketch, "E1161", {"start": v(38, -14.54) * mm, "end": v(38.82, -13.69) * mm});
            skLineSegment(sketch, "E1162", {"start": v(38.82, -13.69) * mm, "end": v(39.2, -13.23) * mm});
            skLineSegment(sketch, "E1163", {"start": v(39.2, -13.23) * mm, "end": v(39.38, -13) * mm});
            skLineSegment(sketch, "E1164", {"start": v(39.38, -13) * mm, "end": v(39.46, -12.9) * mm});
            skLineSegment(sketch, "E1165", {"start": v(39.46, -12.9) * mm, "end": v(41.11, -12.6) * mm});
            skLineSegment(sketch, "E1166", {"start": v(41.11, -12.6) * mm, "end": v(42.86, -12.2) * mm});
            skLineSegment(sketch, "E1167", {"start": v(42.86, -12.2) * mm, "end": v(44.54, -11.7) * mm});
            skLineSegment(sketch, "E1168", {"start": v(44.54, -11.7) * mm, "end": v(47.64, -10.55) * mm});
            skLineSegment(sketch, "E1169", {"start": v(47.64, -10.55) * mm, "end": v(50.3, -9.28) * mm});
            skLineSegment(sketch, "E1170", {"start": v(50.3, -9.28) * mm, "end": v(50.9, -8.95) * mm});
            skLineSegment(sketch, "E1171", {"start": v(50.9, -8.95) * mm, "end": v(51.45, -8.64) * mm});
            skLineSegment(sketch, "E1172", {"start": v(51.45, -8.64) * mm, "end": v(52.45, -8.02) * mm});
            skLineSegment(sketch, "E1173", {"start": v(52.45, -8.02) * mm, "end": v(53.32, -7.46) * mm});
            skLineSegment(sketch, "E1174", {"start": v(53.32, -7.46) * mm, "end": v(54.04, -6.96) * mm});
            skLineSegment(sketch, "E1175", {"start": v(54.04, -6.96) * mm, "end": v(55.03, -6.22) * mm});
            skLineSegment(sketch, "E1176", {"start": v(55.03, -6.22) * mm, "end": v(55.37, -5.96) * mm});
            skLineSegment(sketch, "E1177", {"start": v(55.37, -5.96) * mm, "end": v(54.98, -6.15) * mm});
            skSolve(sketch);
        }
        {
            var Q0;
            Q0=qSketchRegion(id+"F0",true);
            extrude(context, id + "F1", {"entities" : qUnion([Q0]), "depth" : 1 * mm});
        }
    });
